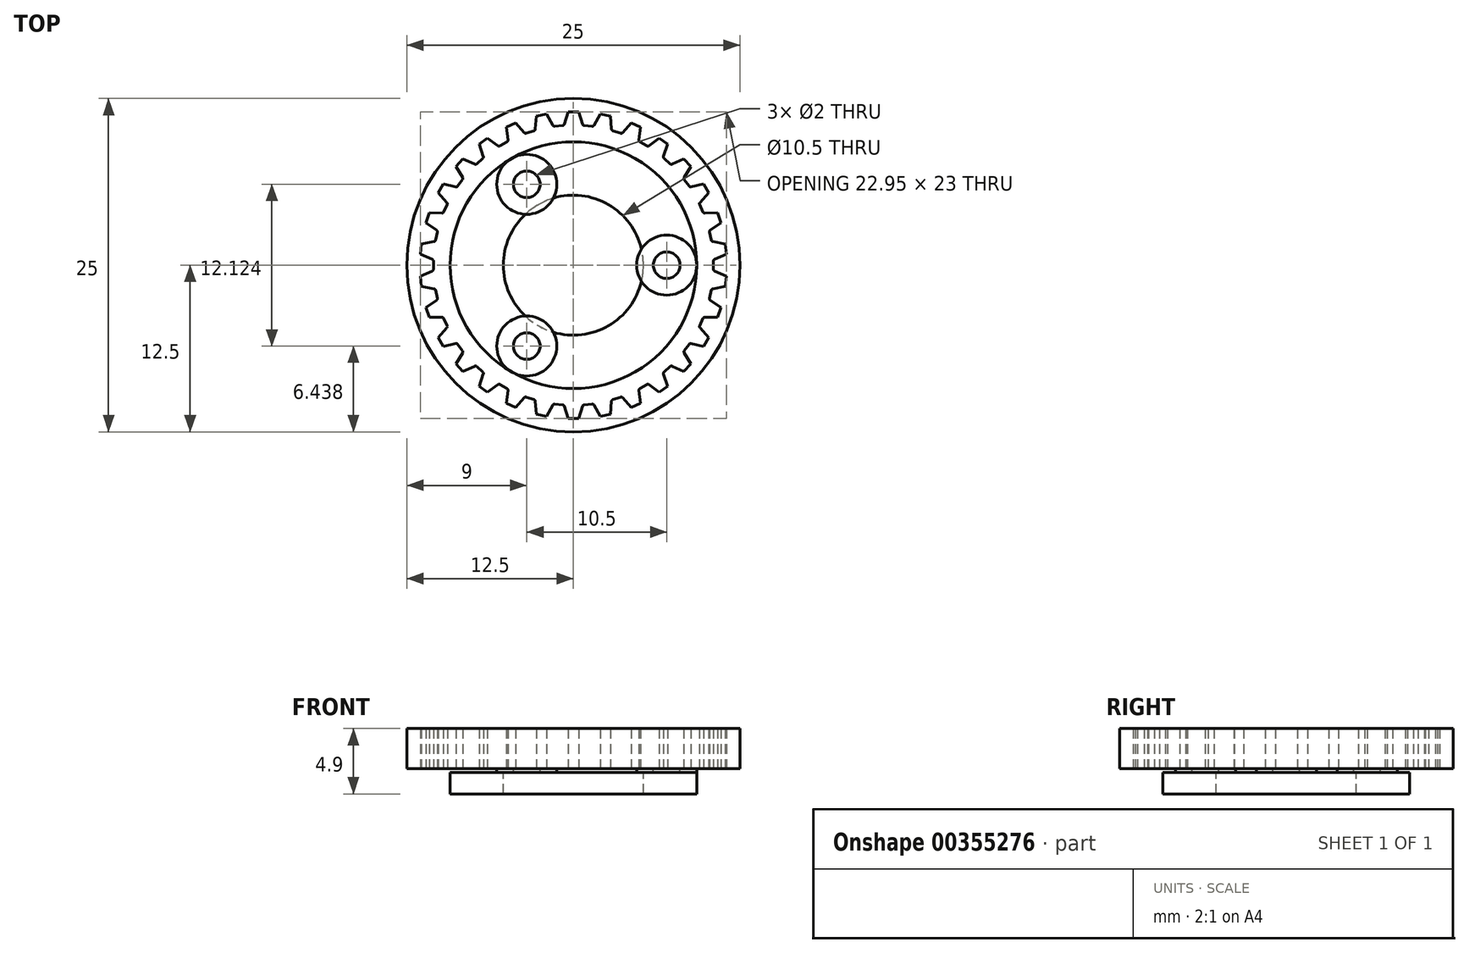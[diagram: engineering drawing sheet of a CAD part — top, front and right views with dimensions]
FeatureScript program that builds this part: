
annotation { "Feature Type Name" : "Feature", "Feature Type Description" : "" }
export const myFeature = defineFeature(function(context is Context, id is Id, definition is map)
    precondition{}
    {
        {
            assignVariable(context, id + "F0", {"name" : "THICK", "anyValue" : 3});
        }
        {
            var Q0;
            Q0=qCreatedBy(makeId("Top.planeOp"),FACE);
            var sketch = newSketch(context, id + "F1", { "sketchPlane" : qUnion([Q0])});
            skCircle(sketch, "E0", {"center": v(0, 0) * mm, "radius": 4 * mm});
            skCircle(sketch, "E1", {"center": v(0, 0) * mm, "radius": 3.5 * mm});
            skCircle(sketch, "E2", {"center": v(0, 0) * mm, "radius": 3 * mm});
            skSolve(sketch);
        }
        {
            var Q0;
            Q0=qCreatedBy(makeId("Top.planeOp"),FACE);
            var sketch = newSketch(context, id + "F2", { "sketchPlane" : qUnion([Q0])});
            skLineSegment(sketch, "E3", {"start": v(0, 0) * mm, "end": v(0, 4.84) * mm, "construction": true});
            skLineSegment(sketch, "E4", {"start": v(1.8, 5.57) * mm, "end": v(0, 0) * mm, "construction": true});
            skLineSegment(sketch, "E5", {"start": v(0.85, 5.38) * mm, "end": v(0, 0) * mm, "construction": true});
            skLineSegment(sketch, "E6", {"start": v(0, 4) * mm, "end": v(0.4, 4) * mm});
            skLineSegment(sketch, "E7", {"start": v(0.56, 3.86) * mm, "end": v(0.6, 2.96) * mm});
            skLineSegment(sketch, "E8", {"start": v(0.6, 2.96) * mm, "end": v(0.93, 2.85) * mm});
            skPoint(sketch, "E9.visualSharp", {"position": v(0.55, 4) * mm});
            skArc(sketch, "E9.filletArc", {"start": v(0.56, 3.86) * mm, "mid": v(0.51, 3.96) * mm, "end": v(0.4, 4) * mm});
            skLineSegment(sketch, "E10.MirrorCS", {"start": v(1.25, 2.75) * mm, "end": v(0.93, 2.85) * mm});
            skLineSegment(sketch, "E11.MirrorCS", {"start": v(2.35, 3.24) * mm, "end": v(2.02, 3.48) * mm});
            skLineSegment(sketch, "E12.MirrorCS", {"start": v(1.82, 3.45) * mm, "end": v(1.25, 2.75) * mm});
            skArc(sketch, "E13.MirrorCS", {"start": v(1.82, 3.45) * mm, "mid": v(1.91, 3.5) * mm, "end": v(2.02, 3.48) * mm});
            skLineSegment(sketch, "E14.1.0", {"start": v(-2.35, 3.24) * mm, "end": v(-2.02, 3.48) * mm});
            skArc(sketch, "E14.1.1", {"start": v(-1.82, 3.45) * mm, "mid": v(-1.91, 3.5) * mm, "end": v(-2.02, 3.48) * mm});
            skLineSegment(sketch, "E14.1.2", {"start": v(-1.82, 3.45) * mm, "end": v(-1.25, 2.75) * mm});
            skLineSegment(sketch, "E14.1.3", {"start": v(-1.25, 2.75) * mm, "end": v(-0.93, 2.85) * mm});
            skLineSegment(sketch, "E14.1.4", {"start": v(-0.6, 2.96) * mm, "end": v(-0.93, 2.85) * mm});
            skLineSegment(sketch, "E14.1.5", {"start": v(-0.56, 3.86) * mm, "end": v(-0.6, 2.96) * mm});
            skLineSegment(sketch, "E14.1.6", {"start": v(0, 4) * mm, "end": v(-0.4, 4) * mm});
            skArc(sketch, "E14.1.7", {"start": v(-0.56, 3.86) * mm, "mid": v(-0.51, 3.96) * mm, "end": v(-0.4, 4) * mm});
            skLineSegment(sketch, "E14.2.0", {"start": v(-3.8, 1.24) * mm, "end": v(-3.68, 1.62) * mm});
            skArc(sketch, "E14.2.1", {"start": v(-3.5, 1.72) * mm, "mid": v(-3.6, 1.7) * mm, "end": v(-3.68, 1.62) * mm});
            skLineSegment(sketch, "E14.2.2", {"start": v(-3.5, 1.72) * mm, "end": v(-2.63, 1.49) * mm});
            skLineSegment(sketch, "E14.2.3", {"start": v(-2.63, 1.49) * mm, "end": v(-2.43, 1.76) * mm});
            skLineSegment(sketch, "E14.2.4", {"start": v(-2.23, 2.04) * mm, "end": v(-2.43, 1.76) * mm});
            skLineSegment(sketch, "E14.2.5", {"start": v(-2.72, 2.8) * mm, "end": v(-2.23, 2.04) * mm});
            skLineSegment(sketch, "E14.2.6", {"start": v(-2.35, 3.24) * mm, "end": v(-2.68, 3) * mm});
            skArc(sketch, "E14.2.7", {"start": v(-2.72, 2.8) * mm, "mid": v(-2.74, 2.9) * mm, "end": v(-2.68, 3) * mm});
            skLineSegment(sketch, "E14.3.0", {"start": v(-3.8, -1.24) * mm, "end": v(-3.93, -0.85) * mm});
            skArc(sketch, "E14.3.1", {"start": v(-3.84, -0.66) * mm, "mid": v(-3.92, -0.74) * mm, "end": v(-3.93, -0.85) * mm});
            skLineSegment(sketch, "E14.3.2", {"start": v(-3.84, -0.66) * mm, "end": v(-3, -0.34) * mm});
            skLineSegment(sketch, "E14.3.3", {"start": v(-3, -0.34) * mm, "end": v(-3, 0) * mm});
            skLineSegment(sketch, "E14.3.4", {"start": v(-3, 0.34) * mm, "end": v(-3, 0) * mm});
            skLineSegment(sketch, "E14.3.5", {"start": v(-3.84, 0.66) * mm, "end": v(-3, 0.34) * mm});
            skLineSegment(sketch, "E14.3.6", {"start": v(-3.8, 1.24) * mm, "end": v(-3.93, 0.85) * mm});
            skArc(sketch, "E14.3.7", {"start": v(-3.84, 0.66) * mm, "mid": v(-3.92, 0.74) * mm, "end": v(-3.93, 0.85) * mm});
            skLineSegment(sketch, "E14.4.0", {"start": v(-2.35, -3.24) * mm, "end": v(-2.68, -3) * mm});
            skArc(sketch, "E14.4.1", {"start": v(-2.72, -2.8) * mm, "mid": v(-2.74, -2.9) * mm, "end": v(-2.68, -3) * mm});
            skLineSegment(sketch, "E14.4.2", {"start": v(-2.72, -2.8) * mm, "end": v(-2.23, -2.04) * mm});
            skLineSegment(sketch, "E14.4.3", {"start": v(-2.23, -2.04) * mm, "end": v(-2.43, -1.76) * mm});
            skLineSegment(sketch, "E14.4.4", {"start": v(-2.63, -1.49) * mm, "end": v(-2.43, -1.76) * mm});
            skLineSegment(sketch, "E14.4.5", {"start": v(-3.5, -1.72) * mm, "end": v(-2.63, -1.49) * mm});
            skLineSegment(sketch, "E14.4.6", {"start": v(-3.8, -1.24) * mm, "end": v(-3.68, -1.62) * mm});
            skArc(sketch, "E14.4.7", {"start": v(-3.5, -1.72) * mm, "mid": v(-3.6, -1.7) * mm, "end": v(-3.68, -1.62) * mm});
            skLineSegment(sketch, "E14.5.0", {"start": v(0, -4) * mm, "end": v(-0.4, -4) * mm});
            skArc(sketch, "E14.5.1", {"start": v(-0.56, -3.86) * mm, "mid": v(-0.51, -3.96) * mm, "end": v(-0.4, -4) * mm});
            skLineSegment(sketch, "E14.5.2", {"start": v(-0.56, -3.86) * mm, "end": v(-0.6, -2.96) * mm});
            skLineSegment(sketch, "E14.5.3", {"start": v(-0.6, -2.96) * mm, "end": v(-0.93, -2.85) * mm});
            skLineSegment(sketch, "E14.5.4", {"start": v(-1.25, -2.75) * mm, "end": v(-0.93, -2.85) * mm});
            skLineSegment(sketch, "E14.5.5", {"start": v(-1.82, -3.45) * mm, "end": v(-1.25, -2.75) * mm});
            skLineSegment(sketch, "E14.5.6", {"start": v(-2.35, -3.24) * mm, "end": v(-2.02, -3.48) * mm});
            skArc(sketch, "E14.5.7", {"start": v(-1.82, -3.45) * mm, "mid": v(-1.91, -3.5) * mm, "end": v(-2.02, -3.48) * mm});
            skLineSegment(sketch, "E14.6.0", {"start": v(2.35, -3.24) * mm, "end": v(2.02, -3.48) * mm});
            skArc(sketch, "E14.6.1", {"start": v(1.82, -3.45) * mm, "mid": v(1.91, -3.5) * mm, "end": v(2.02, -3.48) * mm});
            skLineSegment(sketch, "E14.6.2", {"start": v(1.82, -3.45) * mm, "end": v(1.25, -2.75) * mm});
            skLineSegment(sketch, "E14.6.3", {"start": v(1.25, -2.75) * mm, "end": v(0.93, -2.85) * mm});
            skLineSegment(sketch, "E14.6.4", {"start": v(0.6, -2.96) * mm, "end": v(0.93, -2.85) * mm});
            skLineSegment(sketch, "E14.6.5", {"start": v(0.56, -3.86) * mm, "end": v(0.6, -2.96) * mm});
            skLineSegment(sketch, "E14.6.6", {"start": v(0, -4) * mm, "end": v(0.4, -4) * mm});
            skArc(sketch, "E14.6.7", {"start": v(0.56, -3.86) * mm, "mid": v(0.51, -3.96) * mm, "end": v(0.4, -4) * mm});
            skLineSegment(sketch, "E14.7.0", {"start": v(3.8, -1.24) * mm, "end": v(3.68, -1.62) * mm});
            skArc(sketch, "E14.7.1", {"start": v(3.5, -1.72) * mm, "mid": v(3.6, -1.7) * mm, "end": v(3.68, -1.62) * mm});
            skLineSegment(sketch, "E14.7.2", {"start": v(3.5, -1.72) * mm, "end": v(2.63, -1.49) * mm});
            skLineSegment(sketch, "E14.7.3", {"start": v(2.63, -1.49) * mm, "end": v(2.43, -1.76) * mm});
            skLineSegment(sketch, "E14.7.4", {"start": v(2.23, -2.04) * mm, "end": v(2.43, -1.76) * mm});
            skLineSegment(sketch, "E14.7.5", {"start": v(2.72, -2.8) * mm, "end": v(2.23, -2.04) * mm});
            skLineSegment(sketch, "E14.7.6", {"start": v(2.35, -3.24) * mm, "end": v(2.68, -3) * mm});
            skArc(sketch, "E14.7.7", {"start": v(2.72, -2.8) * mm, "mid": v(2.74, -2.9) * mm, "end": v(2.68, -3) * mm});
            skLineSegment(sketch, "E14.8.0", {"start": v(3.8, 1.24) * mm, "end": v(3.93, 0.85) * mm});
            skArc(sketch, "E14.8.1", {"start": v(3.84, 0.66) * mm, "mid": v(3.92, 0.74) * mm, "end": v(3.93, 0.85) * mm});
            skLineSegment(sketch, "E14.8.2", {"start": v(3.84, 0.66) * mm, "end": v(3, 0.34) * mm});
            skLineSegment(sketch, "E14.8.3", {"start": v(3, 0.34) * mm, "end": v(3, 0) * mm});
            skLineSegment(sketch, "E14.8.4", {"start": v(3, -0.34) * mm, "end": v(3, 0) * mm});
            skLineSegment(sketch, "E14.8.5", {"start": v(3.84, -0.66) * mm, "end": v(3, -0.34) * mm});
            skLineSegment(sketch, "E14.8.6", {"start": v(3.8, -1.24) * mm, "end": v(3.93, -0.85) * mm});
            skArc(sketch, "E14.8.7", {"start": v(3.84, -0.66) * mm, "mid": v(3.92, -0.74) * mm, "end": v(3.93, -0.85) * mm});
            skLineSegment(sketch, "E14.9.0", {"start": v(2.35, 3.24) * mm, "end": v(2.68, 3) * mm});
            skArc(sketch, "E14.9.1", {"start": v(2.72, 2.8) * mm, "mid": v(2.74, 2.9) * mm, "end": v(2.68, 3) * mm});
            skLineSegment(sketch, "E14.9.2", {"start": v(2.72, 2.8) * mm, "end": v(2.23, 2.04) * mm});
            skLineSegment(sketch, "E14.9.3", {"start": v(2.23, 2.04) * mm, "end": v(2.43, 1.76) * mm});
            skLineSegment(sketch, "E14.9.4", {"start": v(2.63, 1.49) * mm, "end": v(2.43, 1.76) * mm});
            skLineSegment(sketch, "E14.9.5", {"start": v(3.5, 1.72) * mm, "end": v(2.63, 1.49) * mm});
            skLineSegment(sketch, "E14.9.6", {"start": v(3.8, 1.24) * mm, "end": v(3.68, 1.62) * mm});
            skArc(sketch, "E14.9.7", {"start": v(3.5, 1.72) * mm, "mid": v(3.6, 1.7) * mm, "end": v(3.68, 1.62) * mm});
            skPoint(sketch, "E14.center", {"position": v(0, 0) * mm});
            skSolve(sketch);
        }
        {
            var Q0;
            Q0=qSketchRegion(id+"F2",true);
            extrude(context, id + "F3", {"entities" : qUnion([Q0]), "depth" : (getVariable(context, 'THICK')) * mm});
        }
        {
            var Q0;
            Q0=makeQuery(id+"F3.opExtrude","CAP_FACE",FACE,{"disambiguationData":[OSD([sQuery(id+"F2.wireOp",EDGE,"E6"),sQuery(id+"F2.wireOp",EDGE,"E7"),sQuery(id+"F2.wireOp",EDGE,"E8"),sQuery(id+"F2.wireOp",EDGE,"E9.filletArc"),sQuery(id+"F2.wireOp",EDGE,"E10.MirrorCS"),sQuery(id+"F2.wireOp",EDGE,"E11.MirrorCS"),sQuery(id+"F2.wireOp",EDGE,"E12.MirrorCS"),sQuery(id+"F2.wireOp",EDGE,"E13.MirrorCS"),sQuery(id+"F2.wireOp",EDGE,"E14.1.0"),sQuery(id+"F2.wireOp",EDGE,"E14.1.1"),sQuery(id+"F2.wireOp",EDGE,"E14.1.2"),sQuery(id+"F2.wireOp",EDGE,"E14.1.3"),sQuery(id+"F2.wireOp",EDGE,"E14.1.4"),sQuery(id+"F2.wireOp",EDGE,"E14.1.5"),sQuery(id+"F2.wireOp",EDGE,"E14.1.6"),sQuery(id+"F2.wireOp",EDGE,"E14.1.7"),sQuery(id+"F2.wireOp",EDGE,"E14.2.0"),sQuery(id+"F2.wireOp",EDGE,"E14.2.1"),sQuery(id+"F2.wireOp",EDGE,"E14.2.2"),sQuery(id+"F2.wireOp",EDGE,"E14.2.3"),sQuery(id+"F2.wireOp",EDGE,"E14.2.4"),sQuery(id+"F2.wireOp",EDGE,"E14.2.5"),sQuery(id+"F2.wireOp",EDGE,"E14.2.6"),sQuery(id+"F2.wireOp",EDGE,"E14.2.7"),sQuery(id+"F2.wireOp",EDGE,"E14.3.0"),sQuery(id+"F2.wireOp",EDGE,"E14.3.1"),sQuery(id+"F2.wireOp",EDGE,"E14.3.2"),sQuery(id+"F2.wireOp",EDGE,"E14.3.3"),sQuery(id+"F2.wireOp",EDGE,"E14.3.4"),sQuery(id+"F2.wireOp",EDGE,"E14.3.5"),sQuery(id+"F2.wireOp",EDGE,"E14.3.6"),sQuery(id+"F2.wireOp",EDGE,"E14.3.7"),sQuery(id+"F2.wireOp",EDGE,"E14.4.0"),sQuery(id+"F2.wireOp",EDGE,"E14.4.1"),sQuery(id+"F2.wireOp",EDGE,"E14.4.2"),sQuery(id+"F2.wireOp",EDGE,"E14.4.3"),sQuery(id+"F2.wireOp",EDGE,"E14.4.4"),sQuery(id+"F2.wireOp",EDGE,"E14.4.5"),sQuery(id+"F2.wireOp",EDGE,"E14.4.6"),sQuery(id+"F2.wireOp",EDGE,"E14.4.7"),sQuery(id+"F2.wireOp",EDGE,"E14.5.0"),sQuery(id+"F2.wireOp",EDGE,"E14.5.1"),sQuery(id+"F2.wireOp",EDGE,"E14.5.2"),sQuery(id+"F2.wireOp",EDGE,"E14.5.3"),sQuery(id+"F2.wireOp",EDGE,"E14.5.4"),sQuery(id+"F2.wireOp",EDGE,"E14.5.5"),sQuery(id+"F2.wireOp",EDGE,"E14.5.6"),sQuery(id+"F2.wireOp",EDGE,"E14.5.7"),sQuery(id+"F2.wireOp",EDGE,"E14.6.0"),sQuery(id+"F2.wireOp",EDGE,"E14.6.1"),sQuery(id+"F2.wireOp",EDGE,"E14.6.2"),sQuery(id+"F2.wireOp",EDGE,"E14.6.3"),sQuery(id+"F2.wireOp",EDGE,"E14.6.4"),sQuery(id+"F2.wireOp",EDGE,"E14.6.5"),sQuery(id+"F2.wireOp",EDGE,"E14.6.6"),sQuery(id+"F2.wireOp",EDGE,"E14.6.7"),sQuery(id+"F2.wireOp",EDGE,"E14.7.0"),sQuery(id+"F2.wireOp",EDGE,"E14.7.1"),sQuery(id+"F2.wireOp",EDGE,"E14.7.2"),sQuery(id+"F2.wireOp",EDGE,"E14.7.3"),sQuery(id+"F2.wireOp",EDGE,"E14.7.4"),sQuery(id+"F2.wireOp",EDGE,"E14.7.5"),sQuery(id+"F2.wireOp",EDGE,"E14.7.6"),sQuery(id+"F2.wireOp",EDGE,"E14.7.7"),sQuery(id+"F2.wireOp",EDGE,"E14.8.0"),sQuery(id+"F2.wireOp",EDGE,"E14.8.1"),sQuery(id+"F2.wireOp",EDGE,"E14.8.2"),sQuery(id+"F2.wireOp",EDGE,"E14.8.3"),sQuery(id+"F2.wireOp",EDGE,"E14.8.4"),sQuery(id+"F2.wireOp",EDGE,"E14.8.5"),sQuery(id+"F2.wireOp",EDGE,"E14.8.6"),sQuery(id+"F2.wireOp",EDGE,"E14.8.7"),sQuery(id+"F2.wireOp",EDGE,"E14.9.0"),sQuery(id+"F2.wireOp",EDGE,"E14.9.1"),sQuery(id+"F2.wireOp",EDGE,"E14.9.2"),sQuery(id+"F2.wireOp",EDGE,"E14.9.3"),sQuery(id+"F2.wireOp",EDGE,"E14.9.4"),sQuery(id+"F2.wireOp",EDGE,"E14.9.5"),sQuery(id+"F2.wireOp",EDGE,"E14.9.6"),sQuery(id+"F2.wireOp",EDGE,"E14.9.7")])],"isStart":true});
            var sketch = newSketch(context, id + "F4", { "sketchPlane" : qUnion([Q0])});
            skCircle(sketch, "E15", {"center": v(0, 0) * mm, "radius": 2.25 * mm});
            skSolve(sketch);
        }
        {
            var Q0;
            Q0=qSketchRegion(id+"F4",true);
            extrude(context, id + "F5", {"entities" : qUnion([Q0]), "operationType" : NewBodyOperationType.ADD, "depth" : 0.3 * mm});
        }
        {
            var Q0;
            Q0=makeQuery(id+"F3.opExtrude","SWEPT_BODY",BODY,{"disambiguationData":[OSD([sQuery(id+"F2.wireOp",EDGE,"E6"),sQuery(id+"F2.wireOp",EDGE,"E7"),sQuery(id+"F2.wireOp",EDGE,"E8"),sQuery(id+"F2.wireOp",EDGE,"E9.filletArc"),sQuery(id+"F2.wireOp",EDGE,"E10.MirrorCS"),sQuery(id+"F2.wireOp",EDGE,"E11.MirrorCS"),sQuery(id+"F2.wireOp",EDGE,"E12.MirrorCS"),sQuery(id+"F2.wireOp",EDGE,"E13.MirrorCS"),sQuery(id+"F2.wireOp",EDGE,"E14.1.0"),sQuery(id+"F2.wireOp",EDGE,"E14.1.1"),sQuery(id+"F2.wireOp",EDGE,"E14.1.2"),sQuery(id+"F2.wireOp",EDGE,"E14.1.3"),sQuery(id+"F2.wireOp",EDGE,"E14.1.4"),sQuery(id+"F2.wireOp",EDGE,"E14.1.5"),sQuery(id+"F2.wireOp",EDGE,"E14.1.6"),sQuery(id+"F2.wireOp",EDGE,"E14.1.7"),sQuery(id+"F2.wireOp",EDGE,"E14.2.0"),sQuery(id+"F2.wireOp",EDGE,"E14.2.1"),sQuery(id+"F2.wireOp",EDGE,"E14.2.2"),sQuery(id+"F2.wireOp",EDGE,"E14.2.3"),sQuery(id+"F2.wireOp",EDGE,"E14.2.4"),sQuery(id+"F2.wireOp",EDGE,"E14.2.5"),sQuery(id+"F2.wireOp",EDGE,"E14.2.6"),sQuery(id+"F2.wireOp",EDGE,"E14.2.7"),sQuery(id+"F2.wireOp",EDGE,"E14.3.0"),sQuery(id+"F2.wireOp",EDGE,"E14.3.1"),sQuery(id+"F2.wireOp",EDGE,"E14.3.2"),sQuery(id+"F2.wireOp",EDGE,"E14.3.3"),sQuery(id+"F2.wireOp",EDGE,"E14.3.4"),sQuery(id+"F2.wireOp",EDGE,"E14.3.5"),sQuery(id+"F2.wireOp",EDGE,"E14.3.6"),sQuery(id+"F2.wireOp",EDGE,"E14.3.7"),sQuery(id+"F2.wireOp",EDGE,"E14.4.0"),sQuery(id+"F2.wireOp",EDGE,"E14.4.1"),sQuery(id+"F2.wireOp",EDGE,"E14.4.2"),sQuery(id+"F2.wireOp",EDGE,"E14.4.3"),sQuery(id+"F2.wireOp",EDGE,"E14.4.4"),sQuery(id+"F2.wireOp",EDGE,"E14.4.5"),sQuery(id+"F2.wireOp",EDGE,"E14.4.6"),sQuery(id+"F2.wireOp",EDGE,"E14.4.7"),sQuery(id+"F2.wireOp",EDGE,"E14.5.0"),sQuery(id+"F2.wireOp",EDGE,"E14.5.1"),sQuery(id+"F2.wireOp",EDGE,"E14.5.2"),sQuery(id+"F2.wireOp",EDGE,"E14.5.3"),sQuery(id+"F2.wireOp",EDGE,"E14.5.4"),sQuery(id+"F2.wireOp",EDGE,"E14.5.5"),sQuery(id+"F2.wireOp",EDGE,"E14.5.6"),sQuery(id+"F2.wireOp",EDGE,"E14.5.7"),sQuery(id+"F2.wireOp",EDGE,"E14.6.0"),sQuery(id+"F2.wireOp",EDGE,"E14.6.1"),sQuery(id+"F2.wireOp",EDGE,"E14.6.2"),sQuery(id+"F2.wireOp",EDGE,"E14.6.3"),sQuery(id+"F2.wireOp",EDGE,"E14.6.4"),sQuery(id+"F2.wireOp",EDGE,"E14.6.5"),sQuery(id+"F2.wireOp",EDGE,"E14.6.6"),sQuery(id+"F2.wireOp",EDGE,"E14.6.7"),sQuery(id+"F2.wireOp",EDGE,"E14.7.0"),sQuery(id+"F2.wireOp",EDGE,"E14.7.1"),sQuery(id+"F2.wireOp",EDGE,"E14.7.2"),sQuery(id+"F2.wireOp",EDGE,"E14.7.3"),sQuery(id+"F2.wireOp",EDGE,"E14.7.4"),sQuery(id+"F2.wireOp",EDGE,"E14.7.5"),sQuery(id+"F2.wireOp",EDGE,"E14.7.6"),sQuery(id+"F2.wireOp",EDGE,"E14.7.7"),sQuery(id+"F2.wireOp",EDGE,"E14.8.0"),sQuery(id+"F2.wireOp",EDGE,"E14.8.1"),sQuery(id+"F2.wireOp",EDGE,"E14.8.2"),sQuery(id+"F2.wireOp",EDGE,"E14.8.3"),sQuery(id+"F2.wireOp",EDGE,"E14.8.4"),sQuery(id+"F2.wireOp",EDGE,"E14.8.5"),sQuery(id+"F2.wireOp",EDGE,"E14.8.6"),sQuery(id+"F2.wireOp",EDGE,"E14.8.7"),sQuery(id+"F2.wireOp",EDGE,"E14.9.0"),sQuery(id+"F2.wireOp",EDGE,"E14.9.1"),sQuery(id+"F2.wireOp",EDGE,"E14.9.2"),sQuery(id+"F2.wireOp",EDGE,"E14.9.3"),sQuery(id+"F2.wireOp",EDGE,"E14.9.4"),sQuery(id+"F2.wireOp",EDGE,"E14.9.5"),sQuery(id+"F2.wireOp",EDGE,"E14.9.6"),sQuery(id+"F2.wireOp",EDGE,"E14.9.7")])]});
            transform(context, id + "F6", {"entities" : qUnion([Q0]), "transformType" : TransformType.COPY});
        }
        {
            var Q0;
            Q0=makeQuery(id+"F3.opExtrude","CAP_FACE",FACE,{"disambiguationData":[OSD([sQuery(id+"F2.wireOp",EDGE,"E6"),sQuery(id+"F2.wireOp",EDGE,"E7"),sQuery(id+"F2.wireOp",EDGE,"E8"),sQuery(id+"F2.wireOp",EDGE,"E9.filletArc"),sQuery(id+"F2.wireOp",EDGE,"E10.MirrorCS"),sQuery(id+"F2.wireOp",EDGE,"E11.MirrorCS"),sQuery(id+"F2.wireOp",EDGE,"E12.MirrorCS"),sQuery(id+"F2.wireOp",EDGE,"E13.MirrorCS"),sQuery(id+"F2.wireOp",EDGE,"E14.1.0"),sQuery(id+"F2.wireOp",EDGE,"E14.1.1"),sQuery(id+"F2.wireOp",EDGE,"E14.1.2"),sQuery(id+"F2.wireOp",EDGE,"E14.1.3"),sQuery(id+"F2.wireOp",EDGE,"E14.1.4"),sQuery(id+"F2.wireOp",EDGE,"E14.1.5"),sQuery(id+"F2.wireOp",EDGE,"E14.1.6"),sQuery(id+"F2.wireOp",EDGE,"E14.1.7"),sQuery(id+"F2.wireOp",EDGE,"E14.2.0"),sQuery(id+"F2.wireOp",EDGE,"E14.2.1"),sQuery(id+"F2.wireOp",EDGE,"E14.2.2"),sQuery(id+"F2.wireOp",EDGE,"E14.2.3"),sQuery(id+"F2.wireOp",EDGE,"E14.2.4"),sQuery(id+"F2.wireOp",EDGE,"E14.2.5"),sQuery(id+"F2.wireOp",EDGE,"E14.2.6"),sQuery(id+"F2.wireOp",EDGE,"E14.2.7"),sQuery(id+"F2.wireOp",EDGE,"E14.3.0"),sQuery(id+"F2.wireOp",EDGE,"E14.3.1"),sQuery(id+"F2.wireOp",EDGE,"E14.3.2"),sQuery(id+"F2.wireOp",EDGE,"E14.3.3"),sQuery(id+"F2.wireOp",EDGE,"E14.3.4"),sQuery(id+"F2.wireOp",EDGE,"E14.3.5"),sQuery(id+"F2.wireOp",EDGE,"E14.3.6"),sQuery(id+"F2.wireOp",EDGE,"E14.3.7"),sQuery(id+"F2.wireOp",EDGE,"E14.4.0"),sQuery(id+"F2.wireOp",EDGE,"E14.4.1"),sQuery(id+"F2.wireOp",EDGE,"E14.4.2"),sQuery(id+"F2.wireOp",EDGE,"E14.4.3"),sQuery(id+"F2.wireOp",EDGE,"E14.4.4"),sQuery(id+"F2.wireOp",EDGE,"E14.4.5"),sQuery(id+"F2.wireOp",EDGE,"E14.4.6"),sQuery(id+"F2.wireOp",EDGE,"E14.4.7"),sQuery(id+"F2.wireOp",EDGE,"E14.5.0"),sQuery(id+"F2.wireOp",EDGE,"E14.5.1"),sQuery(id+"F2.wireOp",EDGE,"E14.5.2"),sQuery(id+"F2.wireOp",EDGE,"E14.5.3"),sQuery(id+"F2.wireOp",EDGE,"E14.5.4"),sQuery(id+"F2.wireOp",EDGE,"E14.5.5"),sQuery(id+"F2.wireOp",EDGE,"E14.5.6"),sQuery(id+"F2.wireOp",EDGE,"E14.5.7"),sQuery(id+"F2.wireOp",EDGE,"E14.6.0"),sQuery(id+"F2.wireOp",EDGE,"E14.6.1"),sQuery(id+"F2.wireOp",EDGE,"E14.6.2"),sQuery(id+"F2.wireOp",EDGE,"E14.6.3"),sQuery(id+"F2.wireOp",EDGE,"E14.6.4"),sQuery(id+"F2.wireOp",EDGE,"E14.6.5"),sQuery(id+"F2.wireOp",EDGE,"E14.6.6"),sQuery(id+"F2.wireOp",EDGE,"E14.6.7"),sQuery(id+"F2.wireOp",EDGE,"E14.7.0"),sQuery(id+"F2.wireOp",EDGE,"E14.7.1"),sQuery(id+"F2.wireOp",EDGE,"E14.7.2"),sQuery(id+"F2.wireOp",EDGE,"E14.7.3"),sQuery(id+"F2.wireOp",EDGE,"E14.7.4"),sQuery(id+"F2.wireOp",EDGE,"E14.7.5"),sQuery(id+"F2.wireOp",EDGE,"E14.7.6"),sQuery(id+"F2.wireOp",EDGE,"E14.7.7"),sQuery(id+"F2.wireOp",EDGE,"E14.8.0"),sQuery(id+"F2.wireOp",EDGE,"E14.8.1"),sQuery(id+"F2.wireOp",EDGE,"E14.8.2"),sQuery(id+"F2.wireOp",EDGE,"E14.8.3"),sQuery(id+"F2.wireOp",EDGE,"E14.8.4"),sQuery(id+"F2.wireOp",EDGE,"E14.8.5"),sQuery(id+"F2.wireOp",EDGE,"E14.8.6"),sQuery(id+"F2.wireOp",EDGE,"E14.8.7"),sQuery(id+"F2.wireOp",EDGE,"E14.9.0"),sQuery(id+"F2.wireOp",EDGE,"E14.9.1"),sQuery(id+"F2.wireOp",EDGE,"E14.9.2"),sQuery(id+"F2.wireOp",EDGE,"E14.9.3"),sQuery(id+"F2.wireOp",EDGE,"E14.9.4"),sQuery(id+"F2.wireOp",EDGE,"E14.9.5"),sQuery(id+"F2.wireOp",EDGE,"E14.9.6"),sQuery(id+"F2.wireOp",EDGE,"E14.9.7")])],"isStart":false});
            var sketch = newSketch(context, id + "F7", { "sketchPlane" : qUnion([Q0])});
            skCircle(sketch, "E16.cCircle", {"center": v(0, 0) * mm, "radius": 0.86 * mm, "construction": true});
            skLineSegment(sketch, "E16.0", {"start": v(0.86, 0.5) * mm, "end": v(0.86, -0.5) * mm});
            skLineSegment(sketch, "E16.1", {"start": v(0.86, -0.5) * mm, "end": v(0, -1) * mm});
            skLineSegment(sketch, "E16.2", {"start": v(0, -1) * mm, "end": v(-0.86, -0.5) * mm});
            skLineSegment(sketch, "E16.3", {"start": v(-0.86, -0.5) * mm, "end": v(-0.86, 0.5) * mm});
            skLineSegment(sketch, "E16.4", {"start": v(-0.86, 0.5) * mm, "end": v(0, 1) * mm});
            skLineSegment(sketch, "E16.5", {"start": v(0, 1) * mm, "end": v(0.86, 0.5) * mm});
            skPoint(sketch, "E16.0.midPoint", {"position": v(0.86, 0) * mm});
            skSolve(sketch);
        }
        {
            var Q0;
            Q0=qSketchRegion(id+"F7",true);
            extrude(context, id + "F8", {"entities" : qUnion([Q0]), "operationType" : NewBodyOperationType.REMOVE, "oppositeDirection" : true, "depth" : 25 * mm});
        }
        {
            var Q0;
            Q0=makeQuery(id+"F3.opExtrude","CAP_FACE",FACE,{"disambiguationData":[OSD([sQuery(id+"F2.wireOp",EDGE,"E6"),sQuery(id+"F2.wireOp",EDGE,"E7"),sQuery(id+"F2.wireOp",EDGE,"E8"),sQuery(id+"F2.wireOp",EDGE,"E9.filletArc"),sQuery(id+"F2.wireOp",EDGE,"E10.MirrorCS"),sQuery(id+"F2.wireOp",EDGE,"E11.MirrorCS"),sQuery(id+"F2.wireOp",EDGE,"E12.MirrorCS"),sQuery(id+"F2.wireOp",EDGE,"E13.MirrorCS"),sQuery(id+"F2.wireOp",EDGE,"E14.1.0"),sQuery(id+"F2.wireOp",EDGE,"E14.1.1"),sQuery(id+"F2.wireOp",EDGE,"E14.1.2"),sQuery(id+"F2.wireOp",EDGE,"E14.1.3"),sQuery(id+"F2.wireOp",EDGE,"E14.1.4"),sQuery(id+"F2.wireOp",EDGE,"E14.1.5"),sQuery(id+"F2.wireOp",EDGE,"E14.1.6"),sQuery(id+"F2.wireOp",EDGE,"E14.1.7"),sQuery(id+"F2.wireOp",EDGE,"E14.2.0"),sQuery(id+"F2.wireOp",EDGE,"E14.2.1"),sQuery(id+"F2.wireOp",EDGE,"E14.2.2"),sQuery(id+"F2.wireOp",EDGE,"E14.2.3"),sQuery(id+"F2.wireOp",EDGE,"E14.2.4"),sQuery(id+"F2.wireOp",EDGE,"E14.2.5"),sQuery(id+"F2.wireOp",EDGE,"E14.2.6"),sQuery(id+"F2.wireOp",EDGE,"E14.2.7"),sQuery(id+"F2.wireOp",EDGE,"E14.3.0"),sQuery(id+"F2.wireOp",EDGE,"E14.3.1"),sQuery(id+"F2.wireOp",EDGE,"E14.3.2"),sQuery(id+"F2.wireOp",EDGE,"E14.3.3"),sQuery(id+"F2.wireOp",EDGE,"E14.3.4"),sQuery(id+"F2.wireOp",EDGE,"E14.3.5"),sQuery(id+"F2.wireOp",EDGE,"E14.3.6"),sQuery(id+"F2.wireOp",EDGE,"E14.3.7"),sQuery(id+"F2.wireOp",EDGE,"E14.4.0"),sQuery(id+"F2.wireOp",EDGE,"E14.4.1"),sQuery(id+"F2.wireOp",EDGE,"E14.4.2"),sQuery(id+"F2.wireOp",EDGE,"E14.4.3"),sQuery(id+"F2.wireOp",EDGE,"E14.4.4"),sQuery(id+"F2.wireOp",EDGE,"E14.4.5"),sQuery(id+"F2.wireOp",EDGE,"E14.4.6"),sQuery(id+"F2.wireOp",EDGE,"E14.4.7"),sQuery(id+"F2.wireOp",EDGE,"E14.5.0"),sQuery(id+"F2.wireOp",EDGE,"E14.5.1"),sQuery(id+"F2.wireOp",EDGE,"E14.5.2"),sQuery(id+"F2.wireOp",EDGE,"E14.5.3"),sQuery(id+"F2.wireOp",EDGE,"E14.5.4"),sQuery(id+"F2.wireOp",EDGE,"E14.5.5"),sQuery(id+"F2.wireOp",EDGE,"E14.5.6"),sQuery(id+"F2.wireOp",EDGE,"E14.5.7"),sQuery(id+"F2.wireOp",EDGE,"E14.6.0"),sQuery(id+"F2.wireOp",EDGE,"E14.6.1"),sQuery(id+"F2.wireOp",EDGE,"E14.6.2"),sQuery(id+"F2.wireOp",EDGE,"E14.6.3"),sQuery(id+"F2.wireOp",EDGE,"E14.6.4"),sQuery(id+"F2.wireOp",EDGE,"E14.6.5"),sQuery(id+"F2.wireOp",EDGE,"E14.6.6"),sQuery(id+"F2.wireOp",EDGE,"E14.6.7"),sQuery(id+"F2.wireOp",EDGE,"E14.7.0"),sQuery(id+"F2.wireOp",EDGE,"E14.7.1"),sQuery(id+"F2.wireOp",EDGE,"E14.7.2"),sQuery(id+"F2.wireOp",EDGE,"E14.7.3"),sQuery(id+"F2.wireOp",EDGE,"E14.7.4"),sQuery(id+"F2.wireOp",EDGE,"E14.7.5"),sQuery(id+"F2.wireOp",EDGE,"E14.7.6"),sQuery(id+"F2.wireOp",EDGE,"E14.7.7"),sQuery(id+"F2.wireOp",EDGE,"E14.8.0"),sQuery(id+"F2.wireOp",EDGE,"E14.8.1"),sQuery(id+"F2.wireOp",EDGE,"E14.8.2"),sQuery(id+"F2.wireOp",EDGE,"E14.8.3"),sQuery(id+"F2.wireOp",EDGE,"E14.8.4"),sQuery(id+"F2.wireOp",EDGE,"E14.8.5"),sQuery(id+"F2.wireOp",EDGE,"E14.8.6"),sQuery(id+"F2.wireOp",EDGE,"E14.8.7"),sQuery(id+"F2.wireOp",EDGE,"E14.9.0"),sQuery(id+"F2.wireOp",EDGE,"E14.9.1"),sQuery(id+"F2.wireOp",EDGE,"E14.9.2"),sQuery(id+"F2.wireOp",EDGE,"E14.9.3"),sQuery(id+"F2.wireOp",EDGE,"E14.9.4"),sQuery(id+"F2.wireOp",EDGE,"E14.9.5"),sQuery(id+"F2.wireOp",EDGE,"E14.9.6"),sQuery(id+"F2.wireOp",EDGE,"E14.9.7")])],"isStart":false});
            var sketch = newSketch(context, id + "F9", { "sketchPlane" : qUnion([Q0])});
            skCircle(sketch, "E17", {"center": v(0, 0) * mm, "radius": 1 * mm});
            skSolve(sketch);
        }
        {
            var Q0;
            Q0=qSketchRegion(id+"F9",true);
            extrude(context, id + "F10", {"entities" : qUnion([Q0]), "operationType" : NewBodyOperationType.REMOVE, "oppositeDirection" : true, "depth" : 25 * mm});
        }
        {
            var Q0;
            Q0=makeQuery(id+"F6.opPattern","COPY",BODY,{"derivedFrom":makeQuery(id+"F3.opExtrude","SWEPT_BODY",BODY,{"disambiguationData":[OSD([sQuery(id+"F2.wireOp",EDGE,"E6"),sQuery(id+"F2.wireOp",EDGE,"E7"),sQuery(id+"F2.wireOp",EDGE,"E8"),sQuery(id+"F2.wireOp",EDGE,"E9.filletArc"),sQuery(id+"F2.wireOp",EDGE,"E10.MirrorCS"),sQuery(id+"F2.wireOp",EDGE,"E11.MirrorCS"),sQuery(id+"F2.wireOp",EDGE,"E12.MirrorCS"),sQuery(id+"F2.wireOp",EDGE,"E13.MirrorCS"),sQuery(id+"F2.wireOp",EDGE,"E14.1.0"),sQuery(id+"F2.wireOp",EDGE,"E14.1.1"),sQuery(id+"F2.wireOp",EDGE,"E14.1.2"),sQuery(id+"F2.wireOp",EDGE,"E14.1.3"),sQuery(id+"F2.wireOp",EDGE,"E14.1.4"),sQuery(id+"F2.wireOp",EDGE,"E14.1.5"),sQuery(id+"F2.wireOp",EDGE,"E14.1.6"),sQuery(id+"F2.wireOp",EDGE,"E14.1.7"),sQuery(id+"F2.wireOp",EDGE,"E14.2.0"),sQuery(id+"F2.wireOp",EDGE,"E14.2.1"),sQuery(id+"F2.wireOp",EDGE,"E14.2.2"),sQuery(id+"F2.wireOp",EDGE,"E14.2.3"),sQuery(id+"F2.wireOp",EDGE,"E14.2.4"),sQuery(id+"F2.wireOp",EDGE,"E14.2.5"),sQuery(id+"F2.wireOp",EDGE,"E14.2.6"),sQuery(id+"F2.wireOp",EDGE,"E14.2.7"),sQuery(id+"F2.wireOp",EDGE,"E14.3.0"),sQuery(id+"F2.wireOp",EDGE,"E14.3.1"),sQuery(id+"F2.wireOp",EDGE,"E14.3.2"),sQuery(id+"F2.wireOp",EDGE,"E14.3.3"),sQuery(id+"F2.wireOp",EDGE,"E14.3.4"),sQuery(id+"F2.wireOp",EDGE,"E14.3.5"),sQuery(id+"F2.wireOp",EDGE,"E14.3.6"),sQuery(id+"F2.wireOp",EDGE,"E14.3.7"),sQuery(id+"F2.wireOp",EDGE,"E14.4.0"),sQuery(id+"F2.wireOp",EDGE,"E14.4.1"),sQuery(id+"F2.wireOp",EDGE,"E14.4.2"),sQuery(id+"F2.wireOp",EDGE,"E14.4.3"),sQuery(id+"F2.wireOp",EDGE,"E14.4.4"),sQuery(id+"F2.wireOp",EDGE,"E14.4.5"),sQuery(id+"F2.wireOp",EDGE,"E14.4.6"),sQuery(id+"F2.wireOp",EDGE,"E14.4.7"),sQuery(id+"F2.wireOp",EDGE,"E14.5.0"),sQuery(id+"F2.wireOp",EDGE,"E14.5.1"),sQuery(id+"F2.wireOp",EDGE,"E14.5.2"),sQuery(id+"F2.wireOp",EDGE,"E14.5.3"),sQuery(id+"F2.wireOp",EDGE,"E14.5.4"),sQuery(id+"F2.wireOp",EDGE,"E14.5.5"),sQuery(id+"F2.wireOp",EDGE,"E14.5.6"),sQuery(id+"F2.wireOp",EDGE,"E14.5.7"),sQuery(id+"F2.wireOp",EDGE,"E14.6.0"),sQuery(id+"F2.wireOp",EDGE,"E14.6.1"),sQuery(id+"F2.wireOp",EDGE,"E14.6.2"),sQuery(id+"F2.wireOp",EDGE,"E14.6.3"),sQuery(id+"F2.wireOp",EDGE,"E14.6.4"),sQuery(id+"F2.wireOp",EDGE,"E14.6.5"),sQuery(id+"F2.wireOp",EDGE,"E14.6.6"),sQuery(id+"F2.wireOp",EDGE,"E14.6.7"),sQuery(id+"F2.wireOp",EDGE,"E14.7.0"),sQuery(id+"F2.wireOp",EDGE,"E14.7.1"),sQuery(id+"F2.wireOp",EDGE,"E14.7.2"),sQuery(id+"F2.wireOp",EDGE,"E14.7.3"),sQuery(id+"F2.wireOp",EDGE,"E14.7.4"),sQuery(id+"F2.wireOp",EDGE,"E14.7.5"),sQuery(id+"F2.wireOp",EDGE,"E14.7.6"),sQuery(id+"F2.wireOp",EDGE,"E14.7.7"),sQuery(id+"F2.wireOp",EDGE,"E14.8.0"),sQuery(id+"F2.wireOp",EDGE,"E14.8.1"),sQuery(id+"F2.wireOp",EDGE,"E14.8.2"),sQuery(id+"F2.wireOp",EDGE,"E14.8.3"),sQuery(id+"F2.wireOp",EDGE,"E14.8.4"),sQuery(id+"F2.wireOp",EDGE,"E14.8.5"),sQuery(id+"F2.wireOp",EDGE,"E14.8.6"),sQuery(id+"F2.wireOp",EDGE,"E14.8.7"),sQuery(id+"F2.wireOp",EDGE,"E14.9.0"),sQuery(id+"F2.wireOp",EDGE,"E14.9.1"),sQuery(id+"F2.wireOp",EDGE,"E14.9.2"),sQuery(id+"F2.wireOp",EDGE,"E14.9.3"),sQuery(id+"F2.wireOp",EDGE,"E14.9.4"),sQuery(id+"F2.wireOp",EDGE,"E14.9.5"),sQuery(id+"F2.wireOp",EDGE,"E14.9.6"),sQuery(id+"F2.wireOp",EDGE,"E14.9.7")])]}),"instanceName":"1"});
            transform(context, id + "F11", {"entities" : qUnion([Q0]), "transformType" : TransformType.COPY});
        }
        {
            var Q0;
            Q0=qCreatedBy(makeId("Top.planeOp"),FACE);
            var sketch = newSketch(context, id + "F12", { "sketchPlane" : qUnion([Q0])});
            skCircle(sketch, "E18", {"center": v(0, 0) * mm, "radius": 10.5 * mm});
            skCircle(sketch, "E19", {"center": v(0, 0) * mm, "radius": 11 * mm});
            skCircle(sketch, "E20.0", {"center": v(0, 0) * mm, "radius": 11.5 * mm});
            skSolve(sketch);
        }
        {
            var Q0;
            Q0=qCreatedBy(makeId("Top.planeOp"),FACE);
            var sketch = newSketch(context, id + "F13", { "sketchPlane" : qUnion([Q0])});
            skLineSegment(sketch, "E21", {"start": v(0, 0) * mm, "end": v(0, 15.18) * mm, "construction": true});
            skLineSegment(sketch, "E22", {"start": v(1.56, 14.86) * mm, "end": v(0, 0) * mm, "construction": true});
            skLineSegment(sketch, "E23", {"start": v(0, 0) * mm, "end": v(0.84, 15.95) * mm, "construction": true});
            skLineSegment(sketch, "E24", {"start": v(0, 11.5) * mm, "end": v(0.39, 11.5) * mm});
            skLineSegment(sketch, "E25", {"start": v(0.39, 11.5) * mm, "end": v(0.67, 10.58) * mm});
            skLineSegment(sketch, "E26", {"start": v(0.8, 10.47) * mm, "end": v(1.1, 10.44) * mm});
            skPoint(sketch, "E27.visualSharp", {"position": v(0.7, 10.48) * mm});
            skArc(sketch, "E27.filletArc", {"start": v(0.67, 10.58) * mm, "mid": v(0.72, 10.5) * mm, "end": v(0.8, 10.47) * mm});
            skLineSegment(sketch, "E28.MirrorCS", {"start": v(1.4, 10.41) * mm, "end": v(1.1, 10.44) * mm});
            skArc(sketch, "E29.MirrorCS", {"start": v(1.54, 10.49) * mm, "mid": v(1.48, 10.43) * mm, "end": v(1.4, 10.41) * mm});
            skLineSegment(sketch, "E30.MirrorCS", {"start": v(2.4, 11.25) * mm, "end": v(2.01, 11.33) * mm});
            skLineSegment(sketch, "E31.MirrorCS", {"start": v(2.01, 11.33) * mm, "end": v(1.54, 10.49) * mm});
            skLineSegment(sketch, "E32.1.0", {"start": v(-2.4, 11.25) * mm, "end": v(-2.01, 11.33) * mm});
            skLineSegment(sketch, "E32.1.1", {"start": v(-2.01, 11.33) * mm, "end": v(-1.54, 10.49) * mm});
            skArc(sketch, "E32.1.2", {"start": v(-1.54, 10.49) * mm, "mid": v(-1.48, 10.43) * mm, "end": v(-1.4, 10.41) * mm});
            skLineSegment(sketch, "E32.1.3", {"start": v(-1.4, 10.41) * mm, "end": v(-1.1, 10.44) * mm});
            skLineSegment(sketch, "E32.1.4", {"start": v(-0.8, 10.47) * mm, "end": v(-1.1, 10.44) * mm});
            skArc(sketch, "E32.1.5", {"start": v(-0.67, 10.58) * mm, "mid": v(-0.72, 10.5) * mm, "end": v(-0.8, 10.47) * mm});
            skLineSegment(sketch, "E32.1.6", {"start": v(-0.39, 11.5) * mm, "end": v(-0.67, 10.58) * mm});
            skLineSegment(sketch, "E32.1.7", {"start": v(0, 11.5) * mm, "end": v(-0.39, 11.5) * mm});
            skLineSegment(sketch, "E32.2.0", {"start": v(-4.68, 10.5) * mm, "end": v(-4.32, 10.66) * mm});
            skLineSegment(sketch, "E32.2.1", {"start": v(-4.32, 10.66) * mm, "end": v(-3.7, 9.94) * mm});
            skArc(sketch, "E32.2.2", {"start": v(-3.7, 9.94) * mm, "mid": v(-3.62, 9.9) * mm, "end": v(-3.53, 9.9) * mm});
            skLineSegment(sketch, "E32.2.3", {"start": v(-3.53, 9.9) * mm, "end": v(-3.24, 9.99) * mm});
            skLineSegment(sketch, "E32.2.4", {"start": v(-2.96, 10.08) * mm, "end": v(-3.24, 9.99) * mm});
            skArc(sketch, "E32.2.5", {"start": v(-2.86, 10.2) * mm, "mid": v(-2.89, 10.13) * mm, "end": v(-2.96, 10.08) * mm});
            skLineSegment(sketch, "E32.2.6", {"start": v(-2.77, 11.17) * mm, "end": v(-2.86, 10.2) * mm});
            skLineSegment(sketch, "E32.2.7", {"start": v(-2.4, 11.25) * mm, "end": v(-2.77, 11.17) * mm});
            skLineSegment(sketch, "E32.3.0", {"start": v(-6.76, 9.3) * mm, "end": v(-6.45, 9.53) * mm});
            skLineSegment(sketch, "E32.3.1", {"start": v(-6.45, 9.53) * mm, "end": v(-5.68, 8.95) * mm});
            skArc(sketch, "E32.3.2", {"start": v(-5.68, 8.95) * mm, "mid": v(-5.6, 8.92) * mm, "end": v(-5.51, 8.94) * mm});
            skLineSegment(sketch, "E32.3.3", {"start": v(-5.51, 8.94) * mm, "end": v(-5.25, 9.1) * mm});
            skLineSegment(sketch, "E32.3.4", {"start": v(-4.99, 9.24) * mm, "end": v(-5.25, 9.1) * mm});
            skArc(sketch, "E32.3.5", {"start": v(-4.92, 9.4) * mm, "mid": v(-4.93, 9.3) * mm, "end": v(-4.99, 9.24) * mm});
            skLineSegment(sketch, "E32.3.6", {"start": v(-5.03, 10.35) * mm, "end": v(-4.92, 9.4) * mm});
            skLineSegment(sketch, "E32.3.7", {"start": v(-4.68, 10.5) * mm, "end": v(-5.03, 10.35) * mm});
            skLineSegment(sketch, "E32.4.0", {"start": v(-8.55, 7.7) * mm, "end": v(-8.29, 7.98) * mm});
            skLineSegment(sketch, "E32.4.1", {"start": v(-8.29, 7.98) * mm, "end": v(-7.41, 7.58) * mm});
            skArc(sketch, "E32.4.2", {"start": v(-7.41, 7.58) * mm, "mid": v(-7.33, 7.56) * mm, "end": v(-7.25, 7.6) * mm});
            skLineSegment(sketch, "E32.4.3", {"start": v(-7.25, 7.6) * mm, "end": v(-7.03, 7.8) * mm});
            skLineSegment(sketch, "E32.4.4", {"start": v(-6.8, 8) * mm, "end": v(-7.03, 7.8) * mm});
            skArc(sketch, "E32.4.5", {"start": v(-6.76, 8.16) * mm, "mid": v(-6.76, 8.08) * mm, "end": v(-6.8, 8) * mm});
            skLineSegment(sketch, "E32.4.6", {"start": v(-7.07, 9.08) * mm, "end": v(-6.76, 8.16) * mm});
            skLineSegment(sketch, "E32.4.7", {"start": v(-6.76, 9.3) * mm, "end": v(-7.07, 9.08) * mm});
            skLineSegment(sketch, "E32.5.0", {"start": v(-9.96, 5.75) * mm, "end": v(-9.77, 6.08) * mm});
            skLineSegment(sketch, "E32.5.1", {"start": v(-9.77, 6.08) * mm, "end": v(-8.83, 5.87) * mm});
            skArc(sketch, "E32.5.2", {"start": v(-8.83, 5.87) * mm, "mid": v(-8.74, 5.88) * mm, "end": v(-8.67, 5.93) * mm});
            skLineSegment(sketch, "E32.5.3", {"start": v(-8.67, 5.93) * mm, "end": v(-8.5, 6.17) * mm});
            skLineSegment(sketch, "E32.5.4", {"start": v(-8.32, 6.42) * mm, "end": v(-8.5, 6.17) * mm});
            skArc(sketch, "E32.5.5", {"start": v(-8.31, 6.58) * mm, "mid": v(-8.29, 6.5) * mm, "end": v(-8.32, 6.42) * mm});
            skLineSegment(sketch, "E32.5.6", {"start": v(-8.8, 7.4) * mm, "end": v(-8.31, 6.58) * mm});
            skLineSegment(sketch, "E32.5.7", {"start": v(-8.55, 7.7) * mm, "end": v(-8.8, 7.4) * mm});
            skLineSegment(sketch, "E32.6.0", {"start": v(-10.94, 3.55) * mm, "end": v(-10.82, 3.92) * mm});
            skLineSegment(sketch, "E32.6.1", {"start": v(-10.82, 3.92) * mm, "end": v(-9.85, 3.9) * mm});
            skArc(sketch, "E32.6.2", {"start": v(-9.85, 3.9) * mm, "mid": v(-9.77, 3.93) * mm, "end": v(-9.71, 4) * mm});
            skLineSegment(sketch, "E32.6.3", {"start": v(-9.71, 4) * mm, "end": v(-9.6, 4.27) * mm});
            skLineSegment(sketch, "E32.6.4", {"start": v(-9.47, 4.55) * mm, "end": v(-9.6, 4.27) * mm});
            skArc(sketch, "E32.6.5", {"start": v(-9.5, 4.7) * mm, "mid": v(-9.46, 4.63) * mm, "end": v(-9.47, 4.55) * mm});
            skLineSegment(sketch, "E32.6.6", {"start": v(-10.15, 5.42) * mm, "end": v(-9.5, 4.7) * mm});
            skLineSegment(sketch, "E32.6.7", {"start": v(-9.96, 5.75) * mm, "end": v(-10.15, 5.42) * mm});
            skLineSegment(sketch, "E32.7.0", {"start": v(-11.44, 1.2) * mm, "end": v(-11.4, 1.59) * mm});
            skLineSegment(sketch, "E32.7.1", {"start": v(-11.4, 1.59) * mm, "end": v(-10.45, 1.77) * mm});
            skArc(sketch, "E32.7.2", {"start": v(-10.45, 1.77) * mm, "mid": v(-10.37, 1.81) * mm, "end": v(-10.33, 1.89) * mm});
            skLineSegment(sketch, "E32.7.3", {"start": v(-10.33, 1.89) * mm, "end": v(-10.27, 2.18) * mm});
            skLineSegment(sketch, "E32.7.4", {"start": v(-10.2, 2.48) * mm, "end": v(-10.27, 2.18) * mm});
            skArc(sketch, "E32.7.5", {"start": v(-10.27, 2.63) * mm, "mid": v(-10.22, 2.56) * mm, "end": v(-10.2, 2.48) * mm});
            skLineSegment(sketch, "E32.7.6", {"start": v(-11.06, 3.19) * mm, "end": v(-10.27, 2.63) * mm});
            skLineSegment(sketch, "E32.7.7", {"start": v(-10.94, 3.55) * mm, "end": v(-11.06, 3.19) * mm});
            skLineSegment(sketch, "E32.8.0", {"start": v(-11.44, -1.2) * mm, "end": v(-11.48, -0.82) * mm});
            skLineSegment(sketch, "E32.8.1", {"start": v(-11.48, -0.82) * mm, "end": v(-10.6, -0.44) * mm});
            skArc(sketch, "E32.8.2", {"start": v(-10.6, -0.44) * mm, "mid": v(-10.52, -0.38) * mm, "end": v(-10.5, -0.3) * mm});
            skLineSegment(sketch, "E32.8.3", {"start": v(-10.5, -0.3) * mm, "end": v(-10.5, 0) * mm});
            skLineSegment(sketch, "E32.8.4", {"start": v(-10.5, 0.3) * mm, "end": v(-10.5, 0) * mm});
            skArc(sketch, "E32.8.5", {"start": v(-10.6, 0.44) * mm, "mid": v(-10.52, 0.38) * mm, "end": v(-10.5, 0.3) * mm});
            skLineSegment(sketch, "E32.8.6", {"start": v(-11.48, 0.82) * mm, "end": v(-10.6, 0.44) * mm});
            skLineSegment(sketch, "E32.8.7", {"start": v(-11.44, 1.2) * mm, "end": v(-11.48, 0.82) * mm});
            skLineSegment(sketch, "E32.9.0", {"start": v(-10.94, -3.55) * mm, "end": v(-11.06, -3.19) * mm});
            skLineSegment(sketch, "E32.9.1", {"start": v(-11.06, -3.19) * mm, "end": v(-10.27, -2.63) * mm});
            skArc(sketch, "E32.9.2", {"start": v(-10.27, -2.63) * mm, "mid": v(-10.22, -2.56) * mm, "end": v(-10.2, -2.48) * mm});
            skLineSegment(sketch, "E32.9.3", {"start": v(-10.2, -2.48) * mm, "end": v(-10.27, -2.18) * mm});
            skLineSegment(sketch, "E32.9.4", {"start": v(-10.33, -1.89) * mm, "end": v(-10.27, -2.18) * mm});
            skArc(sketch, "E32.9.5", {"start": v(-10.45, -1.77) * mm, "mid": v(-10.37, -1.81) * mm, "end": v(-10.33, -1.89) * mm});
            skLineSegment(sketch, "E32.9.6", {"start": v(-11.4, -1.59) * mm, "end": v(-10.45, -1.77) * mm});
            skLineSegment(sketch, "E32.9.7", {"start": v(-11.44, -1.2) * mm, "end": v(-11.4, -1.59) * mm});
            skLineSegment(sketch, "E32.10.0", {"start": v(-9.96, -5.75) * mm, "end": v(-10.15, -5.42) * mm});
            skLineSegment(sketch, "E32.10.1", {"start": v(-10.15, -5.42) * mm, "end": v(-9.5, -4.7) * mm});
            skArc(sketch, "E32.10.2", {"start": v(-9.5, -4.7) * mm, "mid": v(-9.46, -4.63) * mm, "end": v(-9.47, -4.55) * mm});
            skLineSegment(sketch, "E32.10.3", {"start": v(-9.47, -4.55) * mm, "end": v(-9.6, -4.27) * mm});
            skLineSegment(sketch, "E32.10.4", {"start": v(-9.71, -4) * mm, "end": v(-9.6, -4.27) * mm});
            skArc(sketch, "E32.10.5", {"start": v(-9.85, -3.9) * mm, "mid": v(-9.77, -3.93) * mm, "end": v(-9.71, -4) * mm});
            skLineSegment(sketch, "E32.10.6", {"start": v(-10.82, -3.92) * mm, "end": v(-9.85, -3.9) * mm});
            skLineSegment(sketch, "E32.10.7", {"start": v(-10.94, -3.55) * mm, "end": v(-10.82, -3.92) * mm});
            skLineSegment(sketch, "E32.11.0", {"start": v(-8.55, -7.7) * mm, "end": v(-8.8, -7.4) * mm});
            skLineSegment(sketch, "E32.11.1", {"start": v(-8.8, -7.4) * mm, "end": v(-8.31, -6.58) * mm});
            skArc(sketch, "E32.11.2", {"start": v(-8.31, -6.58) * mm, "mid": v(-8.29, -6.5) * mm, "end": v(-8.32, -6.42) * mm});
            skLineSegment(sketch, "E32.11.3", {"start": v(-8.32, -6.42) * mm, "end": v(-8.5, -6.17) * mm});
            skLineSegment(sketch, "E32.11.4", {"start": v(-8.67, -5.93) * mm, "end": v(-8.5, -6.17) * mm});
            skArc(sketch, "E32.11.5", {"start": v(-8.83, -5.87) * mm, "mid": v(-8.74, -5.88) * mm, "end": v(-8.67, -5.93) * mm});
            skLineSegment(sketch, "E32.11.6", {"start": v(-9.77, -6.08) * mm, "end": v(-8.83, -5.87) * mm});
            skLineSegment(sketch, "E32.11.7", {"start": v(-9.96, -5.75) * mm, "end": v(-9.77, -6.08) * mm});
            skLineSegment(sketch, "E32.12.0", {"start": v(-6.76, -9.3) * mm, "end": v(-7.07, -9.08) * mm});
            skLineSegment(sketch, "E32.12.1", {"start": v(-7.07, -9.08) * mm, "end": v(-6.76, -8.16) * mm});
            skArc(sketch, "E32.12.2", {"start": v(-6.76, -8.16) * mm, "mid": v(-6.76, -8.08) * mm, "end": v(-6.8, -8) * mm});
            skLineSegment(sketch, "E32.12.3", {"start": v(-6.8, -8) * mm, "end": v(-7.03, -7.8) * mm});
            skLineSegment(sketch, "E32.12.4", {"start": v(-7.25, -7.6) * mm, "end": v(-7.03, -7.8) * mm});
            skArc(sketch, "E32.12.5", {"start": v(-7.41, -7.58) * mm, "mid": v(-7.33, -7.56) * mm, "end": v(-7.25, -7.6) * mm});
            skLineSegment(sketch, "E32.12.6", {"start": v(-8.29, -7.98) * mm, "end": v(-7.41, -7.58) * mm});
            skLineSegment(sketch, "E32.12.7", {"start": v(-8.55, -7.7) * mm, "end": v(-8.29, -7.98) * mm});
            skLineSegment(sketch, "E32.13.0", {"start": v(-4.68, -10.5) * mm, "end": v(-5.03, -10.35) * mm});
            skLineSegment(sketch, "E32.13.1", {"start": v(-5.03, -10.35) * mm, "end": v(-4.92, -9.4) * mm});
            skArc(sketch, "E32.13.2", {"start": v(-4.92, -9.4) * mm, "mid": v(-4.93, -9.3) * mm, "end": v(-4.99, -9.24) * mm});
            skLineSegment(sketch, "E32.13.3", {"start": v(-4.99, -9.24) * mm, "end": v(-5.25, -9.1) * mm});
            skLineSegment(sketch, "E32.13.4", {"start": v(-5.51, -8.94) * mm, "end": v(-5.25, -9.1) * mm});
            skArc(sketch, "E32.13.5", {"start": v(-5.68, -8.95) * mm, "mid": v(-5.6, -8.92) * mm, "end": v(-5.51, -8.94) * mm});
            skLineSegment(sketch, "E32.13.6", {"start": v(-6.45, -9.53) * mm, "end": v(-5.68, -8.95) * mm});
            skLineSegment(sketch, "E32.13.7", {"start": v(-6.76, -9.3) * mm, "end": v(-6.45, -9.53) * mm});
            skLineSegment(sketch, "E32.14.0", {"start": v(-2.4, -11.25) * mm, "end": v(-2.77, -11.17) * mm});
            skLineSegment(sketch, "E32.14.1", {"start": v(-2.77, -11.17) * mm, "end": v(-2.86, -10.2) * mm});
            skArc(sketch, "E32.14.2", {"start": v(-2.86, -10.2) * mm, "mid": v(-2.89, -10.13) * mm, "end": v(-2.96, -10.08) * mm});
            skLineSegment(sketch, "E32.14.3", {"start": v(-2.96, -10.08) * mm, "end": v(-3.24, -9.99) * mm});
            skLineSegment(sketch, "E32.14.4", {"start": v(-3.53, -9.9) * mm, "end": v(-3.24, -9.99) * mm});
            skArc(sketch, "E32.14.5", {"start": v(-3.7, -9.94) * mm, "mid": v(-3.62, -9.9) * mm, "end": v(-3.53, -9.9) * mm});
            skLineSegment(sketch, "E32.14.6", {"start": v(-4.32, -10.66) * mm, "end": v(-3.7, -9.94) * mm});
            skLineSegment(sketch, "E32.14.7", {"start": v(-4.68, -10.5) * mm, "end": v(-4.32, -10.66) * mm});
            skLineSegment(sketch, "E32.15.0", {"start": v(0, -11.5) * mm, "end": v(-0.39, -11.5) * mm});
            skLineSegment(sketch, "E32.15.1", {"start": v(-0.39, -11.5) * mm, "end": v(-0.67, -10.58) * mm});
            skArc(sketch, "E32.15.2", {"start": v(-0.67, -10.58) * mm, "mid": v(-0.72, -10.5) * mm, "end": v(-0.8, -10.47) * mm});
            skLineSegment(sketch, "E32.15.3", {"start": v(-0.8, -10.47) * mm, "end": v(-1.1, -10.44) * mm});
            skLineSegment(sketch, "E32.15.4", {"start": v(-1.4, -10.41) * mm, "end": v(-1.1, -10.44) * mm});
            skArc(sketch, "E32.15.5", {"start": v(-1.54, -10.49) * mm, "mid": v(-1.48, -10.43) * mm, "end": v(-1.4, -10.41) * mm});
            skLineSegment(sketch, "E32.15.6", {"start": v(-2.01, -11.33) * mm, "end": v(-1.54, -10.49) * mm});
            skLineSegment(sketch, "E32.15.7", {"start": v(-2.4, -11.25) * mm, "end": v(-2.01, -11.33) * mm});
            skLineSegment(sketch, "E32.16.0", {"start": v(2.4, -11.25) * mm, "end": v(2.01, -11.33) * mm});
            skLineSegment(sketch, "E32.16.1", {"start": v(2.01, -11.33) * mm, "end": v(1.54, -10.49) * mm});
            skArc(sketch, "E32.16.2", {"start": v(1.54, -10.49) * mm, "mid": v(1.48, -10.43) * mm, "end": v(1.4, -10.41) * mm});
            skLineSegment(sketch, "E32.16.3", {"start": v(1.4, -10.41) * mm, "end": v(1.1, -10.44) * mm});
            skLineSegment(sketch, "E32.16.4", {"start": v(0.8, -10.47) * mm, "end": v(1.1, -10.44) * mm});
            skArc(sketch, "E32.16.5", {"start": v(0.67, -10.58) * mm, "mid": v(0.72, -10.5) * mm, "end": v(0.8, -10.47) * mm});
            skLineSegment(sketch, "E32.16.6", {"start": v(0.39, -11.5) * mm, "end": v(0.67, -10.58) * mm});
            skLineSegment(sketch, "E32.16.7", {"start": v(0, -11.5) * mm, "end": v(0.39, -11.5) * mm});
            skLineSegment(sketch, "E32.17.0", {"start": v(4.68, -10.5) * mm, "end": v(4.32, -10.66) * mm});
            skLineSegment(sketch, "E32.17.1", {"start": v(4.32, -10.66) * mm, "end": v(3.7, -9.94) * mm});
            skArc(sketch, "E32.17.2", {"start": v(3.7, -9.94) * mm, "mid": v(3.62, -9.9) * mm, "end": v(3.53, -9.9) * mm});
            skLineSegment(sketch, "E32.17.3", {"start": v(3.53, -9.9) * mm, "end": v(3.24, -9.99) * mm});
            skLineSegment(sketch, "E32.17.4", {"start": v(2.96, -10.08) * mm, "end": v(3.24, -9.99) * mm});
            skArc(sketch, "E32.17.5", {"start": v(2.86, -10.2) * mm, "mid": v(2.89, -10.13) * mm, "end": v(2.96, -10.08) * mm});
            skLineSegment(sketch, "E32.17.6", {"start": v(2.77, -11.17) * mm, "end": v(2.86, -10.2) * mm});
            skLineSegment(sketch, "E32.17.7", {"start": v(2.4, -11.25) * mm, "end": v(2.77, -11.17) * mm});
            skLineSegment(sketch, "E32.18.0", {"start": v(6.76, -9.3) * mm, "end": v(6.45, -9.53) * mm});
            skLineSegment(sketch, "E32.18.1", {"start": v(6.45, -9.53) * mm, "end": v(5.68, -8.95) * mm});
            skArc(sketch, "E32.18.2", {"start": v(5.68, -8.95) * mm, "mid": v(5.6, -8.92) * mm, "end": v(5.51, -8.94) * mm});
            skLineSegment(sketch, "E32.18.3", {"start": v(5.51, -8.94) * mm, "end": v(5.25, -9.1) * mm});
            skLineSegment(sketch, "E32.18.4", {"start": v(4.99, -9.24) * mm, "end": v(5.25, -9.1) * mm});
            skArc(sketch, "E32.18.5", {"start": v(4.92, -9.4) * mm, "mid": v(4.93, -9.3) * mm, "end": v(4.99, -9.24) * mm});
            skLineSegment(sketch, "E32.18.6", {"start": v(5.03, -10.35) * mm, "end": v(4.92, -9.4) * mm});
            skLineSegment(sketch, "E32.18.7", {"start": v(4.68, -10.5) * mm, "end": v(5.03, -10.35) * mm});
            skLineSegment(sketch, "E32.19.0", {"start": v(8.55, -7.7) * mm, "end": v(8.29, -7.98) * mm});
            skLineSegment(sketch, "E32.19.1", {"start": v(8.29, -7.98) * mm, "end": v(7.41, -7.58) * mm});
            skArc(sketch, "E32.19.2", {"start": v(7.41, -7.58) * mm, "mid": v(7.33, -7.56) * mm, "end": v(7.25, -7.6) * mm});
            skLineSegment(sketch, "E32.19.3", {"start": v(7.25, -7.6) * mm, "end": v(7.03, -7.8) * mm});
            skLineSegment(sketch, "E32.19.4", {"start": v(6.8, -8) * mm, "end": v(7.03, -7.8) * mm});
            skArc(sketch, "E32.19.5", {"start": v(6.76, -8.16) * mm, "mid": v(6.76, -8.08) * mm, "end": v(6.8, -8) * mm});
            skLineSegment(sketch, "E32.19.6", {"start": v(7.07, -9.08) * mm, "end": v(6.76, -8.16) * mm});
            skLineSegment(sketch, "E32.19.7", {"start": v(6.76, -9.3) * mm, "end": v(7.07, -9.08) * mm});
            skLineSegment(sketch, "E32.20.0", {"start": v(9.96, -5.75) * mm, "end": v(9.77, -6.08) * mm});
            skLineSegment(sketch, "E32.20.1", {"start": v(9.77, -6.08) * mm, "end": v(8.83, -5.87) * mm});
            skArc(sketch, "E32.20.2", {"start": v(8.83, -5.87) * mm, "mid": v(8.74, -5.88) * mm, "end": v(8.67, -5.93) * mm});
            skLineSegment(sketch, "E32.20.3", {"start": v(8.67, -5.93) * mm, "end": v(8.5, -6.17) * mm});
            skLineSegment(sketch, "E32.20.4", {"start": v(8.32, -6.42) * mm, "end": v(8.5, -6.17) * mm});
            skArc(sketch, "E32.20.5", {"start": v(8.31, -6.58) * mm, "mid": v(8.29, -6.5) * mm, "end": v(8.32, -6.42) * mm});
            skLineSegment(sketch, "E32.20.6", {"start": v(8.8, -7.4) * mm, "end": v(8.31, -6.58) * mm});
            skLineSegment(sketch, "E32.20.7", {"start": v(8.55, -7.7) * mm, "end": v(8.8, -7.4) * mm});
            skLineSegment(sketch, "E32.21.0", {"start": v(10.94, -3.55) * mm, "end": v(10.82, -3.92) * mm});
            skLineSegment(sketch, "E32.21.1", {"start": v(10.82, -3.92) * mm, "end": v(9.85, -3.9) * mm});
            skArc(sketch, "E32.21.2", {"start": v(9.85, -3.9) * mm, "mid": v(9.77, -3.93) * mm, "end": v(9.71, -4) * mm});
            skLineSegment(sketch, "E32.21.3", {"start": v(9.71, -4) * mm, "end": v(9.6, -4.27) * mm});
            skLineSegment(sketch, "E32.21.4", {"start": v(9.47, -4.55) * mm, "end": v(9.6, -4.27) * mm});
            skArc(sketch, "E32.21.5", {"start": v(9.5, -4.7) * mm, "mid": v(9.46, -4.63) * mm, "end": v(9.47, -4.55) * mm});
            skLineSegment(sketch, "E32.21.6", {"start": v(10.15, -5.42) * mm, "end": v(9.5, -4.7) * mm});
            skLineSegment(sketch, "E32.21.7", {"start": v(9.96, -5.75) * mm, "end": v(10.15, -5.42) * mm});
            skLineSegment(sketch, "E32.22.0", {"start": v(11.44, -1.2) * mm, "end": v(11.4, -1.59) * mm});
            skLineSegment(sketch, "E32.22.1", {"start": v(11.4, -1.59) * mm, "end": v(10.45, -1.77) * mm});
            skArc(sketch, "E32.22.2", {"start": v(10.45, -1.77) * mm, "mid": v(10.37, -1.81) * mm, "end": v(10.33, -1.89) * mm});
            skLineSegment(sketch, "E32.22.3", {"start": v(10.33, -1.89) * mm, "end": v(10.27, -2.18) * mm});
            skLineSegment(sketch, "E32.22.4", {"start": v(10.2, -2.48) * mm, "end": v(10.27, -2.18) * mm});
            skArc(sketch, "E32.22.5", {"start": v(10.27, -2.63) * mm, "mid": v(10.22, -2.56) * mm, "end": v(10.2, -2.48) * mm});
            skLineSegment(sketch, "E32.22.6", {"start": v(11.06, -3.19) * mm, "end": v(10.27, -2.63) * mm});
            skLineSegment(sketch, "E32.22.7", {"start": v(10.94, -3.55) * mm, "end": v(11.06, -3.19) * mm});
            skLineSegment(sketch, "E32.23.0", {"start": v(11.44, 1.2) * mm, "end": v(11.48, 0.82) * mm});
            skLineSegment(sketch, "E32.23.1", {"start": v(11.48, 0.82) * mm, "end": v(10.6, 0.44) * mm});
            skArc(sketch, "E32.23.2", {"start": v(10.6, 0.44) * mm, "mid": v(10.52, 0.38) * mm, "end": v(10.5, 0.3) * mm});
            skLineSegment(sketch, "E32.23.3", {"start": v(10.5, 0.3) * mm, "end": v(10.5, 0) * mm});
            skLineSegment(sketch, "E32.23.4", {"start": v(10.5, -0.3) * mm, "end": v(10.5, 0) * mm});
            skArc(sketch, "E32.23.5", {"start": v(10.6, -0.44) * mm, "mid": v(10.52, -0.38) * mm, "end": v(10.5, -0.3) * mm});
            skLineSegment(sketch, "E32.23.6", {"start": v(11.48, -0.82) * mm, "end": v(10.6, -0.44) * mm});
            skLineSegment(sketch, "E32.23.7", {"start": v(11.44, -1.2) * mm, "end": v(11.48, -0.82) * mm});
            skLineSegment(sketch, "E32.24.0", {"start": v(10.94, 3.55) * mm, "end": v(11.06, 3.19) * mm});
            skLineSegment(sketch, "E32.24.1", {"start": v(11.06, 3.19) * mm, "end": v(10.27, 2.63) * mm});
            skArc(sketch, "E32.24.2", {"start": v(10.27, 2.63) * mm, "mid": v(10.22, 2.56) * mm, "end": v(10.2, 2.48) * mm});
            skLineSegment(sketch, "E32.24.3", {"start": v(10.2, 2.48) * mm, "end": v(10.27, 2.18) * mm});
            skLineSegment(sketch, "E32.24.4", {"start": v(10.33, 1.89) * mm, "end": v(10.27, 2.18) * mm});
            skArc(sketch, "E32.24.5", {"start": v(10.45, 1.77) * mm, "mid": v(10.37, 1.81) * mm, "end": v(10.33, 1.89) * mm});
            skLineSegment(sketch, "E32.24.6", {"start": v(11.4, 1.59) * mm, "end": v(10.45, 1.77) * mm});
            skLineSegment(sketch, "E32.24.7", {"start": v(11.44, 1.2) * mm, "end": v(11.4, 1.59) * mm});
            skLineSegment(sketch, "E32.25.0", {"start": v(9.96, 5.75) * mm, "end": v(10.15, 5.42) * mm});
            skLineSegment(sketch, "E32.25.1", {"start": v(10.15, 5.42) * mm, "end": v(9.5, 4.7) * mm});
            skArc(sketch, "E32.25.2", {"start": v(9.5, 4.7) * mm, "mid": v(9.46, 4.63) * mm, "end": v(9.47, 4.55) * mm});
            skLineSegment(sketch, "E32.25.3", {"start": v(9.47, 4.55) * mm, "end": v(9.6, 4.27) * mm});
            skLineSegment(sketch, "E32.25.4", {"start": v(9.71, 4) * mm, "end": v(9.6, 4.27) * mm});
            skArc(sketch, "E32.25.5", {"start": v(9.85, 3.9) * mm, "mid": v(9.77, 3.93) * mm, "end": v(9.71, 4) * mm});
            skLineSegment(sketch, "E32.25.6", {"start": v(10.82, 3.92) * mm, "end": v(9.85, 3.9) * mm});
            skLineSegment(sketch, "E32.25.7", {"start": v(10.94, 3.55) * mm, "end": v(10.82, 3.92) * mm});
            skLineSegment(sketch, "E32.26.0", {"start": v(8.55, 7.7) * mm, "end": v(8.8, 7.4) * mm});
            skLineSegment(sketch, "E32.26.1", {"start": v(8.8, 7.4) * mm, "end": v(8.31, 6.58) * mm});
            skArc(sketch, "E32.26.2", {"start": v(8.31, 6.58) * mm, "mid": v(8.29, 6.5) * mm, "end": v(8.32, 6.42) * mm});
            skLineSegment(sketch, "E32.26.3", {"start": v(8.32, 6.42) * mm, "end": v(8.5, 6.17) * mm});
            skLineSegment(sketch, "E32.26.4", {"start": v(8.67, 5.93) * mm, "end": v(8.5, 6.17) * mm});
            skArc(sketch, "E32.26.5", {"start": v(8.83, 5.87) * mm, "mid": v(8.74, 5.88) * mm, "end": v(8.67, 5.93) * mm});
            skLineSegment(sketch, "E32.26.6", {"start": v(9.77, 6.08) * mm, "end": v(8.83, 5.87) * mm});
            skLineSegment(sketch, "E32.26.7", {"start": v(9.96, 5.75) * mm, "end": v(9.77, 6.08) * mm});
            skLineSegment(sketch, "E32.27.0", {"start": v(6.76, 9.3) * mm, "end": v(7.07, 9.08) * mm});
            skLineSegment(sketch, "E32.27.1", {"start": v(7.07, 9.08) * mm, "end": v(6.76, 8.16) * mm});
            skArc(sketch, "E32.27.2", {"start": v(6.76, 8.16) * mm, "mid": v(6.76, 8.08) * mm, "end": v(6.8, 8) * mm});
            skLineSegment(sketch, "E32.27.3", {"start": v(6.8, 8) * mm, "end": v(7.03, 7.8) * mm});
            skLineSegment(sketch, "E32.27.4", {"start": v(7.25, 7.6) * mm, "end": v(7.03, 7.8) * mm});
            skArc(sketch, "E32.27.5", {"start": v(7.41, 7.58) * mm, "mid": v(7.33, 7.56) * mm, "end": v(7.25, 7.6) * mm});
            skLineSegment(sketch, "E32.27.6", {"start": v(8.29, 7.98) * mm, "end": v(7.41, 7.58) * mm});
            skLineSegment(sketch, "E32.27.7", {"start": v(8.55, 7.7) * mm, "end": v(8.29, 7.98) * mm});
            skLineSegment(sketch, "E32.28.0", {"start": v(4.68, 10.5) * mm, "end": v(5.03, 10.35) * mm});
            skLineSegment(sketch, "E32.28.1", {"start": v(5.03, 10.35) * mm, "end": v(4.92, 9.4) * mm});
            skArc(sketch, "E32.28.2", {"start": v(4.92, 9.4) * mm, "mid": v(4.93, 9.3) * mm, "end": v(4.99, 9.24) * mm});
            skLineSegment(sketch, "E32.28.3", {"start": v(4.99, 9.24) * mm, "end": v(5.25, 9.1) * mm});
            skLineSegment(sketch, "E32.28.4", {"start": v(5.51, 8.94) * mm, "end": v(5.25, 9.1) * mm});
            skArc(sketch, "E32.28.5", {"start": v(5.68, 8.95) * mm, "mid": v(5.6, 8.92) * mm, "end": v(5.51, 8.94) * mm});
            skLineSegment(sketch, "E32.28.6", {"start": v(6.45, 9.53) * mm, "end": v(5.68, 8.95) * mm});
            skLineSegment(sketch, "E32.28.7", {"start": v(6.76, 9.3) * mm, "end": v(6.45, 9.53) * mm});
            skLineSegment(sketch, "E32.29.0", {"start": v(2.4, 11.25) * mm, "end": v(2.77, 11.17) * mm});
            skLineSegment(sketch, "E32.29.1", {"start": v(2.77, 11.17) * mm, "end": v(2.86, 10.2) * mm});
            skArc(sketch, "E32.29.2", {"start": v(2.86, 10.2) * mm, "mid": v(2.89, 10.13) * mm, "end": v(2.96, 10.08) * mm});
            skLineSegment(sketch, "E32.29.3", {"start": v(2.96, 10.08) * mm, "end": v(3.24, 9.99) * mm});
            skLineSegment(sketch, "E32.29.4", {"start": v(3.53, 9.9) * mm, "end": v(3.24, 9.99) * mm});
            skArc(sketch, "E32.29.5", {"start": v(3.7, 9.94) * mm, "mid": v(3.62, 9.9) * mm, "end": v(3.53, 9.9) * mm});
            skLineSegment(sketch, "E32.29.6", {"start": v(4.32, 10.66) * mm, "end": v(3.7, 9.94) * mm});
            skLineSegment(sketch, "E32.29.7", {"start": v(4.68, 10.5) * mm, "end": v(4.32, 10.66) * mm});
            skPoint(sketch, "E32.center", {"position": v(0, 0) * mm});
            skSolve(sketch);
        }
        {
            var Q0;
            Q0=qCreatedBy(makeId("Top.planeOp"),FACE);
            var sketch = newSketch(context, id + "F14", { "sketchPlane" : qUnion([Q0])});
            skCircle(sketch, "E33", {"center": v(0, 0) * mm, "radius": 12.5 * mm});
            skSolve(sketch);
        }
        {
            var Q0;
            Q0=qSketchRegion(id+"F14",true);
            extrude(context, id + "F15", {"entities" : qUnion([Q0]), "depth" : (getVariable(context, 'THICK')) * mm});
        }
        {
            var Q0;
            Q0=qSketchRegion(id+"F13",true);
            extrude(context, id + "F16", {"entities" : qUnion([Q0]), "operationType" : NewBodyOperationType.REMOVE, "depth" : 25 * mm});
        }
        {
            var Q0;
            Q0=qCreatedBy(makeId("Front.planeOp"),FACE);
            var sketch = newSketch(context, id + "F17", { "sketchPlane" : qUnion([Q0])});
            skLineSegment(sketch, "E34", {"start": v(0, 0) * mm, "end": v(0, 5.62) * mm});
            skSolve(sketch);
        }
        {
            var Q0;
            Q0=makeQuery(id+"F15.opExtrude","SWEPT_BODY",BODY,{"disambiguationData":[OSD([sQuery(id+"F14.wireOp",EDGE,"E33")])]});
            var Q1;
            Q1=sQuery(id+"F17.wireOp",EDGE,"E34");
            transform(context, id + "F18", {"entities" : qUnion([Q0]), "transformType" : TransformType.ROTATION, "transformAxis" : qUnion([Q1]), "angle" : 0 * degree, "makeCopy" : false});
        }
        {
            var Q0;
            Q0=qCreatedBy(makeId("Top.planeOp"),FACE);
            var sketch = newSketch(context, id + "F19", { "sketchPlane" : qUnion([Q0])});
            skCircle(sketch, "E35.cCircle", {"center": v(0, 0) * mm, "radius": 3.5 * mm, "construction": true});
            skLineSegment(sketch, "E35.0", {"start": v(-3.5, -6.06) * mm, "end": v(-3.5, 6.06) * mm});
            skLineSegment(sketch, "E35.1", {"start": v(-3.5, 6.06) * mm, "end": v(7, 0) * mm});
            skLineSegment(sketch, "E35.2", {"start": v(7, 0) * mm, "end": v(-3.5, -6.06) * mm});
            skPoint(sketch, "E35.0.midPoint", {"position": v(-3.5, 0) * mm});
            skLineSegment(sketch, "E36", {"start": v(0, 0) * mm, "end": v(7, 0) * mm});
            skLineSegment(sketch, "E37", {"start": v(0, 0) * mm, "end": v(-3.5, 6.06) * mm});
            skLineSegment(sketch, "E38", {"start": v(0, 0) * mm, "end": v(-3.5, -6.06) * mm});
            skSolve(sketch);
        }
        {
            var Q0;
            Q0=makeQuery(id+"F3.opExtrude","SWEPT_BODY",BODY,{"disambiguationData":[OSD([sQuery(id+"F2.wireOp",EDGE,"E6"),sQuery(id+"F2.wireOp",EDGE,"E7"),sQuery(id+"F2.wireOp",EDGE,"E8"),sQuery(id+"F2.wireOp",EDGE,"E9.filletArc"),sQuery(id+"F2.wireOp",EDGE,"E10.MirrorCS"),sQuery(id+"F2.wireOp",EDGE,"E11.MirrorCS"),sQuery(id+"F2.wireOp",EDGE,"E12.MirrorCS"),sQuery(id+"F2.wireOp",EDGE,"E13.MirrorCS"),sQuery(id+"F2.wireOp",EDGE,"E14.1.0"),sQuery(id+"F2.wireOp",EDGE,"E14.1.1"),sQuery(id+"F2.wireOp",EDGE,"E14.1.2"),sQuery(id+"F2.wireOp",EDGE,"E14.1.3"),sQuery(id+"F2.wireOp",EDGE,"E14.1.4"),sQuery(id+"F2.wireOp",EDGE,"E14.1.5"),sQuery(id+"F2.wireOp",EDGE,"E14.1.6"),sQuery(id+"F2.wireOp",EDGE,"E14.1.7"),sQuery(id+"F2.wireOp",EDGE,"E14.2.0"),sQuery(id+"F2.wireOp",EDGE,"E14.2.1"),sQuery(id+"F2.wireOp",EDGE,"E14.2.2"),sQuery(id+"F2.wireOp",EDGE,"E14.2.3"),sQuery(id+"F2.wireOp",EDGE,"E14.2.4"),sQuery(id+"F2.wireOp",EDGE,"E14.2.5"),sQuery(id+"F2.wireOp",EDGE,"E14.2.6"),sQuery(id+"F2.wireOp",EDGE,"E14.2.7"),sQuery(id+"F2.wireOp",EDGE,"E14.3.0"),sQuery(id+"F2.wireOp",EDGE,"E14.3.1"),sQuery(id+"F2.wireOp",EDGE,"E14.3.2"),sQuery(id+"F2.wireOp",EDGE,"E14.3.3"),sQuery(id+"F2.wireOp",EDGE,"E14.3.4"),sQuery(id+"F2.wireOp",EDGE,"E14.3.5"),sQuery(id+"F2.wireOp",EDGE,"E14.3.6"),sQuery(id+"F2.wireOp",EDGE,"E14.3.7"),sQuery(id+"F2.wireOp",EDGE,"E14.4.0"),sQuery(id+"F2.wireOp",EDGE,"E14.4.1"),sQuery(id+"F2.wireOp",EDGE,"E14.4.2"),sQuery(id+"F2.wireOp",EDGE,"E14.4.3"),sQuery(id+"F2.wireOp",EDGE,"E14.4.4"),sQuery(id+"F2.wireOp",EDGE,"E14.4.5"),sQuery(id+"F2.wireOp",EDGE,"E14.4.6"),sQuery(id+"F2.wireOp",EDGE,"E14.4.7"),sQuery(id+"F2.wireOp",EDGE,"E14.5.0"),sQuery(id+"F2.wireOp",EDGE,"E14.5.1"),sQuery(id+"F2.wireOp",EDGE,"E14.5.2"),sQuery(id+"F2.wireOp",EDGE,"E14.5.3"),sQuery(id+"F2.wireOp",EDGE,"E14.5.4"),sQuery(id+"F2.wireOp",EDGE,"E14.5.5"),sQuery(id+"F2.wireOp",EDGE,"E14.5.6"),sQuery(id+"F2.wireOp",EDGE,"E14.5.7"),sQuery(id+"F2.wireOp",EDGE,"E14.6.0"),sQuery(id+"F2.wireOp",EDGE,"E14.6.1"),sQuery(id+"F2.wireOp",EDGE,"E14.6.2"),sQuery(id+"F2.wireOp",EDGE,"E14.6.3"),sQuery(id+"F2.wireOp",EDGE,"E14.6.4"),sQuery(id+"F2.wireOp",EDGE,"E14.6.5"),sQuery(id+"F2.wireOp",EDGE,"E14.6.6"),sQuery(id+"F2.wireOp",EDGE,"E14.6.7"),sQuery(id+"F2.wireOp",EDGE,"E14.7.0"),sQuery(id+"F2.wireOp",EDGE,"E14.7.1"),sQuery(id+"F2.wireOp",EDGE,"E14.7.2"),sQuery(id+"F2.wireOp",EDGE,"E14.7.3"),sQuery(id+"F2.wireOp",EDGE,"E14.7.4"),sQuery(id+"F2.wireOp",EDGE,"E14.7.5"),sQuery(id+"F2.wireOp",EDGE,"E14.7.6"),sQuery(id+"F2.wireOp",EDGE,"E14.7.7"),sQuery(id+"F2.wireOp",EDGE,"E14.8.0"),sQuery(id+"F2.wireOp",EDGE,"E14.8.1"),sQuery(id+"F2.wireOp",EDGE,"E14.8.2"),sQuery(id+"F2.wireOp",EDGE,"E14.8.3"),sQuery(id+"F2.wireOp",EDGE,"E14.8.4"),sQuery(id+"F2.wireOp",EDGE,"E14.8.5"),sQuery(id+"F2.wireOp",EDGE,"E14.8.6"),sQuery(id+"F2.wireOp",EDGE,"E14.8.7"),sQuery(id+"F2.wireOp",EDGE,"E14.9.0"),sQuery(id+"F2.wireOp",EDGE,"E14.9.1"),sQuery(id+"F2.wireOp",EDGE,"E14.9.2"),sQuery(id+"F2.wireOp",EDGE,"E14.9.3"),sQuery(id+"F2.wireOp",EDGE,"E14.9.4"),sQuery(id+"F2.wireOp",EDGE,"E14.9.5"),sQuery(id+"F2.wireOp",EDGE,"E14.9.6"),sQuery(id+"F2.wireOp",EDGE,"E14.9.7")])]});
            var Q1;
            Q1=sQuery(id+"F17.wireOp",EDGE,"E34");
            transform(context, id + "F20", {"entities" : qUnion([Q0]), "transformType" : TransformType.ROTATION, "transformAxis" : qUnion([Q1]), "angle" : 0 * degree, "makeCopy" : false});
        }
        {
            var Q0;
            Q0=makeQuery(id+"F6.opPattern","COPY",BODY,{"derivedFrom":makeQuery(id+"F3.opExtrude","SWEPT_BODY",BODY,{"disambiguationData":[OSD([sQuery(id+"F2.wireOp",EDGE,"E6"),sQuery(id+"F2.wireOp",EDGE,"E7"),sQuery(id+"F2.wireOp",EDGE,"E8"),sQuery(id+"F2.wireOp",EDGE,"E9.filletArc"),sQuery(id+"F2.wireOp",EDGE,"E10.MirrorCS"),sQuery(id+"F2.wireOp",EDGE,"E11.MirrorCS"),sQuery(id+"F2.wireOp",EDGE,"E12.MirrorCS"),sQuery(id+"F2.wireOp",EDGE,"E13.MirrorCS"),sQuery(id+"F2.wireOp",EDGE,"E14.1.0"),sQuery(id+"F2.wireOp",EDGE,"E14.1.1"),sQuery(id+"F2.wireOp",EDGE,"E14.1.2"),sQuery(id+"F2.wireOp",EDGE,"E14.1.3"),sQuery(id+"F2.wireOp",EDGE,"E14.1.4"),sQuery(id+"F2.wireOp",EDGE,"E14.1.5"),sQuery(id+"F2.wireOp",EDGE,"E14.1.6"),sQuery(id+"F2.wireOp",EDGE,"E14.1.7"),sQuery(id+"F2.wireOp",EDGE,"E14.2.0"),sQuery(id+"F2.wireOp",EDGE,"E14.2.1"),sQuery(id+"F2.wireOp",EDGE,"E14.2.2"),sQuery(id+"F2.wireOp",EDGE,"E14.2.3"),sQuery(id+"F2.wireOp",EDGE,"E14.2.4"),sQuery(id+"F2.wireOp",EDGE,"E14.2.5"),sQuery(id+"F2.wireOp",EDGE,"E14.2.6"),sQuery(id+"F2.wireOp",EDGE,"E14.2.7"),sQuery(id+"F2.wireOp",EDGE,"E14.3.0"),sQuery(id+"F2.wireOp",EDGE,"E14.3.1"),sQuery(id+"F2.wireOp",EDGE,"E14.3.2"),sQuery(id+"F2.wireOp",EDGE,"E14.3.3"),sQuery(id+"F2.wireOp",EDGE,"E14.3.4"),sQuery(id+"F2.wireOp",EDGE,"E14.3.5"),sQuery(id+"F2.wireOp",EDGE,"E14.3.6"),sQuery(id+"F2.wireOp",EDGE,"E14.3.7"),sQuery(id+"F2.wireOp",EDGE,"E14.4.0"),sQuery(id+"F2.wireOp",EDGE,"E14.4.1"),sQuery(id+"F2.wireOp",EDGE,"E14.4.2"),sQuery(id+"F2.wireOp",EDGE,"E14.4.3"),sQuery(id+"F2.wireOp",EDGE,"E14.4.4"),sQuery(id+"F2.wireOp",EDGE,"E14.4.5"),sQuery(id+"F2.wireOp",EDGE,"E14.4.6"),sQuery(id+"F2.wireOp",EDGE,"E14.4.7"),sQuery(id+"F2.wireOp",EDGE,"E14.5.0"),sQuery(id+"F2.wireOp",EDGE,"E14.5.1"),sQuery(id+"F2.wireOp",EDGE,"E14.5.2"),sQuery(id+"F2.wireOp",EDGE,"E14.5.3"),sQuery(id+"F2.wireOp",EDGE,"E14.5.4"),sQuery(id+"F2.wireOp",EDGE,"E14.5.5"),sQuery(id+"F2.wireOp",EDGE,"E14.5.6"),sQuery(id+"F2.wireOp",EDGE,"E14.5.7"),sQuery(id+"F2.wireOp",EDGE,"E14.6.0"),sQuery(id+"F2.wireOp",EDGE,"E14.6.1"),sQuery(id+"F2.wireOp",EDGE,"E14.6.2"),sQuery(id+"F2.wireOp",EDGE,"E14.6.3"),sQuery(id+"F2.wireOp",EDGE,"E14.6.4"),sQuery(id+"F2.wireOp",EDGE,"E14.6.5"),sQuery(id+"F2.wireOp",EDGE,"E14.6.6"),sQuery(id+"F2.wireOp",EDGE,"E14.6.7"),sQuery(id+"F2.wireOp",EDGE,"E14.7.0"),sQuery(id+"F2.wireOp",EDGE,"E14.7.1"),sQuery(id+"F2.wireOp",EDGE,"E14.7.2"),sQuery(id+"F2.wireOp",EDGE,"E14.7.3"),sQuery(id+"F2.wireOp",EDGE,"E14.7.4"),sQuery(id+"F2.wireOp",EDGE,"E14.7.5"),sQuery(id+"F2.wireOp",EDGE,"E14.7.6"),sQuery(id+"F2.wireOp",EDGE,"E14.7.7"),sQuery(id+"F2.wireOp",EDGE,"E14.8.0"),sQuery(id+"F2.wireOp",EDGE,"E14.8.1"),sQuery(id+"F2.wireOp",EDGE,"E14.8.2"),sQuery(id+"F2.wireOp",EDGE,"E14.8.3"),sQuery(id+"F2.wireOp",EDGE,"E14.8.4"),sQuery(id+"F2.wireOp",EDGE,"E14.8.5"),sQuery(id+"F2.wireOp",EDGE,"E14.8.6"),sQuery(id+"F2.wireOp",EDGE,"E14.8.7"),sQuery(id+"F2.wireOp",EDGE,"E14.9.0"),sQuery(id+"F2.wireOp",EDGE,"E14.9.1"),sQuery(id+"F2.wireOp",EDGE,"E14.9.2"),sQuery(id+"F2.wireOp",EDGE,"E14.9.3"),sQuery(id+"F2.wireOp",EDGE,"E14.9.4"),sQuery(id+"F2.wireOp",EDGE,"E14.9.5"),sQuery(id+"F2.wireOp",EDGE,"E14.9.6"),sQuery(id+"F2.wireOp",EDGE,"E14.9.7")])]}),"instanceName":"1"});
            var Q1;
            Q1=sQuery(id+"F17.wireOp",EDGE,"E34");
            transform(context, id + "F21", {"entities" : qUnion([Q0]), "transformType" : TransformType.ROTATION, "transformAxis" : qUnion([Q1]), "angle" : 12 * degree, "makeCopy" : false});
        }
        {
            var Q0;
            Q0=makeQuery(id+"F11.opPattern","COPY",BODY,{"derivedFrom":makeQuery(id+"F6.opPattern","COPY",BODY,{"derivedFrom":makeQuery(id+"F3.opExtrude","SWEPT_BODY",BODY,{"disambiguationData":[OSD([sQuery(id+"F2.wireOp",EDGE,"E6"),sQuery(id+"F2.wireOp",EDGE,"E7"),sQuery(id+"F2.wireOp",EDGE,"E8"),sQuery(id+"F2.wireOp",EDGE,"E9.filletArc"),sQuery(id+"F2.wireOp",EDGE,"E10.MirrorCS"),sQuery(id+"F2.wireOp",EDGE,"E11.MirrorCS"),sQuery(id+"F2.wireOp",EDGE,"E12.MirrorCS"),sQuery(id+"F2.wireOp",EDGE,"E13.MirrorCS"),sQuery(id+"F2.wireOp",EDGE,"E14.1.0"),sQuery(id+"F2.wireOp",EDGE,"E14.1.1"),sQuery(id+"F2.wireOp",EDGE,"E14.1.2"),sQuery(id+"F2.wireOp",EDGE,"E14.1.3"),sQuery(id+"F2.wireOp",EDGE,"E14.1.4"),sQuery(id+"F2.wireOp",EDGE,"E14.1.5"),sQuery(id+"F2.wireOp",EDGE,"E14.1.6"),sQuery(id+"F2.wireOp",EDGE,"E14.1.7"),sQuery(id+"F2.wireOp",EDGE,"E14.2.0"),sQuery(id+"F2.wireOp",EDGE,"E14.2.1"),sQuery(id+"F2.wireOp",EDGE,"E14.2.2"),sQuery(id+"F2.wireOp",EDGE,"E14.2.3"),sQuery(id+"F2.wireOp",EDGE,"E14.2.4"),sQuery(id+"F2.wireOp",EDGE,"E14.2.5"),sQuery(id+"F2.wireOp",EDGE,"E14.2.6"),sQuery(id+"F2.wireOp",EDGE,"E14.2.7"),sQuery(id+"F2.wireOp",EDGE,"E14.3.0"),sQuery(id+"F2.wireOp",EDGE,"E14.3.1"),sQuery(id+"F2.wireOp",EDGE,"E14.3.2"),sQuery(id+"F2.wireOp",EDGE,"E14.3.3"),sQuery(id+"F2.wireOp",EDGE,"E14.3.4"),sQuery(id+"F2.wireOp",EDGE,"E14.3.5"),sQuery(id+"F2.wireOp",EDGE,"E14.3.6"),sQuery(id+"F2.wireOp",EDGE,"E14.3.7"),sQuery(id+"F2.wireOp",EDGE,"E14.4.0"),sQuery(id+"F2.wireOp",EDGE,"E14.4.1"),sQuery(id+"F2.wireOp",EDGE,"E14.4.2"),sQuery(id+"F2.wireOp",EDGE,"E14.4.3"),sQuery(id+"F2.wireOp",EDGE,"E14.4.4"),sQuery(id+"F2.wireOp",EDGE,"E14.4.5"),sQuery(id+"F2.wireOp",EDGE,"E14.4.6"),sQuery(id+"F2.wireOp",EDGE,"E14.4.7"),sQuery(id+"F2.wireOp",EDGE,"E14.5.0"),sQuery(id+"F2.wireOp",EDGE,"E14.5.1"),sQuery(id+"F2.wireOp",EDGE,"E14.5.2"),sQuery(id+"F2.wireOp",EDGE,"E14.5.3"),sQuery(id+"F2.wireOp",EDGE,"E14.5.4"),sQuery(id+"F2.wireOp",EDGE,"E14.5.5"),sQuery(id+"F2.wireOp",EDGE,"E14.5.6"),sQuery(id+"F2.wireOp",EDGE,"E14.5.7"),sQuery(id+"F2.wireOp",EDGE,"E14.6.0"),sQuery(id+"F2.wireOp",EDGE,"E14.6.1"),sQuery(id+"F2.wireOp",EDGE,"E14.6.2"),sQuery(id+"F2.wireOp",EDGE,"E14.6.3"),sQuery(id+"F2.wireOp",EDGE,"E14.6.4"),sQuery(id+"F2.wireOp",EDGE,"E14.6.5"),sQuery(id+"F2.wireOp",EDGE,"E14.6.6"),sQuery(id+"F2.wireOp",EDGE,"E14.6.7"),sQuery(id+"F2.wireOp",EDGE,"E14.7.0"),sQuery(id+"F2.wireOp",EDGE,"E14.7.1"),sQuery(id+"F2.wireOp",EDGE,"E14.7.2"),sQuery(id+"F2.wireOp",EDGE,"E14.7.3"),sQuery(id+"F2.wireOp",EDGE,"E14.7.4"),sQuery(id+"F2.wireOp",EDGE,"E14.7.5"),sQuery(id+"F2.wireOp",EDGE,"E14.7.6"),sQuery(id+"F2.wireOp",EDGE,"E14.7.7"),sQuery(id+"F2.wireOp",EDGE,"E14.8.0"),sQuery(id+"F2.wireOp",EDGE,"E14.8.1"),sQuery(id+"F2.wireOp",EDGE,"E14.8.2"),sQuery(id+"F2.wireOp",EDGE,"E14.8.3"),sQuery(id+"F2.wireOp",EDGE,"E14.8.4"),sQuery(id+"F2.wireOp",EDGE,"E14.8.5"),sQuery(id+"F2.wireOp",EDGE,"E14.8.6"),sQuery(id+"F2.wireOp",EDGE,"E14.8.7"),sQuery(id+"F2.wireOp",EDGE,"E14.9.0"),sQuery(id+"F2.wireOp",EDGE,"E14.9.1"),sQuery(id+"F2.wireOp",EDGE,"E14.9.2"),sQuery(id+"F2.wireOp",EDGE,"E14.9.3"),sQuery(id+"F2.wireOp",EDGE,"E14.9.4"),sQuery(id+"F2.wireOp",EDGE,"E14.9.5"),sQuery(id+"F2.wireOp",EDGE,"E14.9.6"),sQuery(id+"F2.wireOp",EDGE,"E14.9.7")])]}),"instanceName":"1"}),"instanceName":"1"});
            var Q1;
            Q1=sQuery(id+"F17.wireOp",EDGE,"E34");
            transform(context, id + "F22", {"entities" : qUnion([Q0]), "transformType" : TransformType.ROTATION, "transformAxis" : qUnion([Q1]), "angle" : 24 * degree, "makeCopy" : false});
        }
        {
            var Q0;
            Q0=makeQuery(id+"F3.opExtrude","SWEPT_BODY",BODY,{"disambiguationData":[OSD([sQuery(id+"F2.wireOp",EDGE,"E6"),sQuery(id+"F2.wireOp",EDGE,"E7"),sQuery(id+"F2.wireOp",EDGE,"E8"),sQuery(id+"F2.wireOp",EDGE,"E9.filletArc"),sQuery(id+"F2.wireOp",EDGE,"E10.MirrorCS"),sQuery(id+"F2.wireOp",EDGE,"E11.MirrorCS"),sQuery(id+"F2.wireOp",EDGE,"E12.MirrorCS"),sQuery(id+"F2.wireOp",EDGE,"E13.MirrorCS"),sQuery(id+"F2.wireOp",EDGE,"E14.1.0"),sQuery(id+"F2.wireOp",EDGE,"E14.1.1"),sQuery(id+"F2.wireOp",EDGE,"E14.1.2"),sQuery(id+"F2.wireOp",EDGE,"E14.1.3"),sQuery(id+"F2.wireOp",EDGE,"E14.1.4"),sQuery(id+"F2.wireOp",EDGE,"E14.1.5"),sQuery(id+"F2.wireOp",EDGE,"E14.1.6"),sQuery(id+"F2.wireOp",EDGE,"E14.1.7"),sQuery(id+"F2.wireOp",EDGE,"E14.2.0"),sQuery(id+"F2.wireOp",EDGE,"E14.2.1"),sQuery(id+"F2.wireOp",EDGE,"E14.2.2"),sQuery(id+"F2.wireOp",EDGE,"E14.2.3"),sQuery(id+"F2.wireOp",EDGE,"E14.2.4"),sQuery(id+"F2.wireOp",EDGE,"E14.2.5"),sQuery(id+"F2.wireOp",EDGE,"E14.2.6"),sQuery(id+"F2.wireOp",EDGE,"E14.2.7"),sQuery(id+"F2.wireOp",EDGE,"E14.3.0"),sQuery(id+"F2.wireOp",EDGE,"E14.3.1"),sQuery(id+"F2.wireOp",EDGE,"E14.3.2"),sQuery(id+"F2.wireOp",EDGE,"E14.3.3"),sQuery(id+"F2.wireOp",EDGE,"E14.3.4"),sQuery(id+"F2.wireOp",EDGE,"E14.3.5"),sQuery(id+"F2.wireOp",EDGE,"E14.3.6"),sQuery(id+"F2.wireOp",EDGE,"E14.3.7"),sQuery(id+"F2.wireOp",EDGE,"E14.4.0"),sQuery(id+"F2.wireOp",EDGE,"E14.4.1"),sQuery(id+"F2.wireOp",EDGE,"E14.4.2"),sQuery(id+"F2.wireOp",EDGE,"E14.4.3"),sQuery(id+"F2.wireOp",EDGE,"E14.4.4"),sQuery(id+"F2.wireOp",EDGE,"E14.4.5"),sQuery(id+"F2.wireOp",EDGE,"E14.4.6"),sQuery(id+"F2.wireOp",EDGE,"E14.4.7"),sQuery(id+"F2.wireOp",EDGE,"E14.5.0"),sQuery(id+"F2.wireOp",EDGE,"E14.5.1"),sQuery(id+"F2.wireOp",EDGE,"E14.5.2"),sQuery(id+"F2.wireOp",EDGE,"E14.5.3"),sQuery(id+"F2.wireOp",EDGE,"E14.5.4"),sQuery(id+"F2.wireOp",EDGE,"E14.5.5"),sQuery(id+"F2.wireOp",EDGE,"E14.5.6"),sQuery(id+"F2.wireOp",EDGE,"E14.5.7"),sQuery(id+"F2.wireOp",EDGE,"E14.6.0"),sQuery(id+"F2.wireOp",EDGE,"E14.6.1"),sQuery(id+"F2.wireOp",EDGE,"E14.6.2"),sQuery(id+"F2.wireOp",EDGE,"E14.6.3"),sQuery(id+"F2.wireOp",EDGE,"E14.6.4"),sQuery(id+"F2.wireOp",EDGE,"E14.6.5"),sQuery(id+"F2.wireOp",EDGE,"E14.6.6"),sQuery(id+"F2.wireOp",EDGE,"E14.6.7"),sQuery(id+"F2.wireOp",EDGE,"E14.7.0"),sQuery(id+"F2.wireOp",EDGE,"E14.7.1"),sQuery(id+"F2.wireOp",EDGE,"E14.7.2"),sQuery(id+"F2.wireOp",EDGE,"E14.7.3"),sQuery(id+"F2.wireOp",EDGE,"E14.7.4"),sQuery(id+"F2.wireOp",EDGE,"E14.7.5"),sQuery(id+"F2.wireOp",EDGE,"E14.7.6"),sQuery(id+"F2.wireOp",EDGE,"E14.7.7"),sQuery(id+"F2.wireOp",EDGE,"E14.8.0"),sQuery(id+"F2.wireOp",EDGE,"E14.8.1"),sQuery(id+"F2.wireOp",EDGE,"E14.8.2"),sQuery(id+"F2.wireOp",EDGE,"E14.8.3"),sQuery(id+"F2.wireOp",EDGE,"E14.8.4"),sQuery(id+"F2.wireOp",EDGE,"E14.8.5"),sQuery(id+"F2.wireOp",EDGE,"E14.8.6"),sQuery(id+"F2.wireOp",EDGE,"E14.8.7"),sQuery(id+"F2.wireOp",EDGE,"E14.9.0"),sQuery(id+"F2.wireOp",EDGE,"E14.9.1"),sQuery(id+"F2.wireOp",EDGE,"E14.9.2"),sQuery(id+"F2.wireOp",EDGE,"E14.9.3"),sQuery(id+"F2.wireOp",EDGE,"E14.9.4"),sQuery(id+"F2.wireOp",EDGE,"E14.9.5"),sQuery(id+"F2.wireOp",EDGE,"E14.9.6"),sQuery(id+"F2.wireOp",EDGE,"E14.9.7")])]});
            var Q1;
            Q1=sQuery(id+"F19.wireOp",EDGE,"E36");
            transform(context, id + "F23", {"entities" : qUnion([Q0]), "transformType" : TransformType.TRANSLATION_ENTITY, "oppositeDirectionEntity" : false, "transformLine" : qUnion([Q1]), "makeCopy" : false});
        }
        {
            var Q0;
            Q0=makeQuery(id+"F6.opPattern","COPY",BODY,{"derivedFrom":makeQuery(id+"F3.opExtrude","SWEPT_BODY",BODY,{"disambiguationData":[OSD([sQuery(id+"F2.wireOp",EDGE,"E6"),sQuery(id+"F2.wireOp",EDGE,"E7"),sQuery(id+"F2.wireOp",EDGE,"E8"),sQuery(id+"F2.wireOp",EDGE,"E9.filletArc"),sQuery(id+"F2.wireOp",EDGE,"E10.MirrorCS"),sQuery(id+"F2.wireOp",EDGE,"E11.MirrorCS"),sQuery(id+"F2.wireOp",EDGE,"E12.MirrorCS"),sQuery(id+"F2.wireOp",EDGE,"E13.MirrorCS"),sQuery(id+"F2.wireOp",EDGE,"E14.1.0"),sQuery(id+"F2.wireOp",EDGE,"E14.1.1"),sQuery(id+"F2.wireOp",EDGE,"E14.1.2"),sQuery(id+"F2.wireOp",EDGE,"E14.1.3"),sQuery(id+"F2.wireOp",EDGE,"E14.1.4"),sQuery(id+"F2.wireOp",EDGE,"E14.1.5"),sQuery(id+"F2.wireOp",EDGE,"E14.1.6"),sQuery(id+"F2.wireOp",EDGE,"E14.1.7"),sQuery(id+"F2.wireOp",EDGE,"E14.2.0"),sQuery(id+"F2.wireOp",EDGE,"E14.2.1"),sQuery(id+"F2.wireOp",EDGE,"E14.2.2"),sQuery(id+"F2.wireOp",EDGE,"E14.2.3"),sQuery(id+"F2.wireOp",EDGE,"E14.2.4"),sQuery(id+"F2.wireOp",EDGE,"E14.2.5"),sQuery(id+"F2.wireOp",EDGE,"E14.2.6"),sQuery(id+"F2.wireOp",EDGE,"E14.2.7"),sQuery(id+"F2.wireOp",EDGE,"E14.3.0"),sQuery(id+"F2.wireOp",EDGE,"E14.3.1"),sQuery(id+"F2.wireOp",EDGE,"E14.3.2"),sQuery(id+"F2.wireOp",EDGE,"E14.3.3"),sQuery(id+"F2.wireOp",EDGE,"E14.3.4"),sQuery(id+"F2.wireOp",EDGE,"E14.3.5"),sQuery(id+"F2.wireOp",EDGE,"E14.3.6"),sQuery(id+"F2.wireOp",EDGE,"E14.3.7"),sQuery(id+"F2.wireOp",EDGE,"E14.4.0"),sQuery(id+"F2.wireOp",EDGE,"E14.4.1"),sQuery(id+"F2.wireOp",EDGE,"E14.4.2"),sQuery(id+"F2.wireOp",EDGE,"E14.4.3"),sQuery(id+"F2.wireOp",EDGE,"E14.4.4"),sQuery(id+"F2.wireOp",EDGE,"E14.4.5"),sQuery(id+"F2.wireOp",EDGE,"E14.4.6"),sQuery(id+"F2.wireOp",EDGE,"E14.4.7"),sQuery(id+"F2.wireOp",EDGE,"E14.5.0"),sQuery(id+"F2.wireOp",EDGE,"E14.5.1"),sQuery(id+"F2.wireOp",EDGE,"E14.5.2"),sQuery(id+"F2.wireOp",EDGE,"E14.5.3"),sQuery(id+"F2.wireOp",EDGE,"E14.5.4"),sQuery(id+"F2.wireOp",EDGE,"E14.5.5"),sQuery(id+"F2.wireOp",EDGE,"E14.5.6"),sQuery(id+"F2.wireOp",EDGE,"E14.5.7"),sQuery(id+"F2.wireOp",EDGE,"E14.6.0"),sQuery(id+"F2.wireOp",EDGE,"E14.6.1"),sQuery(id+"F2.wireOp",EDGE,"E14.6.2"),sQuery(id+"F2.wireOp",EDGE,"E14.6.3"),sQuery(id+"F2.wireOp",EDGE,"E14.6.4"),sQuery(id+"F2.wireOp",EDGE,"E14.6.5"),sQuery(id+"F2.wireOp",EDGE,"E14.6.6"),sQuery(id+"F2.wireOp",EDGE,"E14.6.7"),sQuery(id+"F2.wireOp",EDGE,"E14.7.0"),sQuery(id+"F2.wireOp",EDGE,"E14.7.1"),sQuery(id+"F2.wireOp",EDGE,"E14.7.2"),sQuery(id+"F2.wireOp",EDGE,"E14.7.3"),sQuery(id+"F2.wireOp",EDGE,"E14.7.4"),sQuery(id+"F2.wireOp",EDGE,"E14.7.5"),sQuery(id+"F2.wireOp",EDGE,"E14.7.6"),sQuery(id+"F2.wireOp",EDGE,"E14.7.7"),sQuery(id+"F2.wireOp",EDGE,"E14.8.0"),sQuery(id+"F2.wireOp",EDGE,"E14.8.1"),sQuery(id+"F2.wireOp",EDGE,"E14.8.2"),sQuery(id+"F2.wireOp",EDGE,"E14.8.3"),sQuery(id+"F2.wireOp",EDGE,"E14.8.4"),sQuery(id+"F2.wireOp",EDGE,"E14.8.5"),sQuery(id+"F2.wireOp",EDGE,"E14.8.6"),sQuery(id+"F2.wireOp",EDGE,"E14.8.7"),sQuery(id+"F2.wireOp",EDGE,"E14.9.0"),sQuery(id+"F2.wireOp",EDGE,"E14.9.1"),sQuery(id+"F2.wireOp",EDGE,"E14.9.2"),sQuery(id+"F2.wireOp",EDGE,"E14.9.3"),sQuery(id+"F2.wireOp",EDGE,"E14.9.4"),sQuery(id+"F2.wireOp",EDGE,"E14.9.5"),sQuery(id+"F2.wireOp",EDGE,"E14.9.6"),sQuery(id+"F2.wireOp",EDGE,"E14.9.7")])]}),"instanceName":"1"});
            var Q1;
            Q1=sQuery(id+"F19.wireOp",EDGE,"E37");
            transform(context, id + "F24", {"entities" : qUnion([Q0]), "transformType" : TransformType.TRANSLATION_ENTITY, "oppositeDirectionEntity" : false, "transformLine" : qUnion([Q1]), "makeCopy" : false});
        }
        {
            var Q0;
            Q0=makeQuery(id+"F11.opPattern","COPY",BODY,{"derivedFrom":makeQuery(id+"F6.opPattern","COPY",BODY,{"derivedFrom":makeQuery(id+"F3.opExtrude","SWEPT_BODY",BODY,{"disambiguationData":[OSD([sQuery(id+"F2.wireOp",EDGE,"E6"),sQuery(id+"F2.wireOp",EDGE,"E7"),sQuery(id+"F2.wireOp",EDGE,"E8"),sQuery(id+"F2.wireOp",EDGE,"E9.filletArc"),sQuery(id+"F2.wireOp",EDGE,"E10.MirrorCS"),sQuery(id+"F2.wireOp",EDGE,"E11.MirrorCS"),sQuery(id+"F2.wireOp",EDGE,"E12.MirrorCS"),sQuery(id+"F2.wireOp",EDGE,"E13.MirrorCS"),sQuery(id+"F2.wireOp",EDGE,"E14.1.0"),sQuery(id+"F2.wireOp",EDGE,"E14.1.1"),sQuery(id+"F2.wireOp",EDGE,"E14.1.2"),sQuery(id+"F2.wireOp",EDGE,"E14.1.3"),sQuery(id+"F2.wireOp",EDGE,"E14.1.4"),sQuery(id+"F2.wireOp",EDGE,"E14.1.5"),sQuery(id+"F2.wireOp",EDGE,"E14.1.6"),sQuery(id+"F2.wireOp",EDGE,"E14.1.7"),sQuery(id+"F2.wireOp",EDGE,"E14.2.0"),sQuery(id+"F2.wireOp",EDGE,"E14.2.1"),sQuery(id+"F2.wireOp",EDGE,"E14.2.2"),sQuery(id+"F2.wireOp",EDGE,"E14.2.3"),sQuery(id+"F2.wireOp",EDGE,"E14.2.4"),sQuery(id+"F2.wireOp",EDGE,"E14.2.5"),sQuery(id+"F2.wireOp",EDGE,"E14.2.6"),sQuery(id+"F2.wireOp",EDGE,"E14.2.7"),sQuery(id+"F2.wireOp",EDGE,"E14.3.0"),sQuery(id+"F2.wireOp",EDGE,"E14.3.1"),sQuery(id+"F2.wireOp",EDGE,"E14.3.2"),sQuery(id+"F2.wireOp",EDGE,"E14.3.3"),sQuery(id+"F2.wireOp",EDGE,"E14.3.4"),sQuery(id+"F2.wireOp",EDGE,"E14.3.5"),sQuery(id+"F2.wireOp",EDGE,"E14.3.6"),sQuery(id+"F2.wireOp",EDGE,"E14.3.7"),sQuery(id+"F2.wireOp",EDGE,"E14.4.0"),sQuery(id+"F2.wireOp",EDGE,"E14.4.1"),sQuery(id+"F2.wireOp",EDGE,"E14.4.2"),sQuery(id+"F2.wireOp",EDGE,"E14.4.3"),sQuery(id+"F2.wireOp",EDGE,"E14.4.4"),sQuery(id+"F2.wireOp",EDGE,"E14.4.5"),sQuery(id+"F2.wireOp",EDGE,"E14.4.6"),sQuery(id+"F2.wireOp",EDGE,"E14.4.7"),sQuery(id+"F2.wireOp",EDGE,"E14.5.0"),sQuery(id+"F2.wireOp",EDGE,"E14.5.1"),sQuery(id+"F2.wireOp",EDGE,"E14.5.2"),sQuery(id+"F2.wireOp",EDGE,"E14.5.3"),sQuery(id+"F2.wireOp",EDGE,"E14.5.4"),sQuery(id+"F2.wireOp",EDGE,"E14.5.5"),sQuery(id+"F2.wireOp",EDGE,"E14.5.6"),sQuery(id+"F2.wireOp",EDGE,"E14.5.7"),sQuery(id+"F2.wireOp",EDGE,"E14.6.0"),sQuery(id+"F2.wireOp",EDGE,"E14.6.1"),sQuery(id+"F2.wireOp",EDGE,"E14.6.2"),sQuery(id+"F2.wireOp",EDGE,"E14.6.3"),sQuery(id+"F2.wireOp",EDGE,"E14.6.4"),sQuery(id+"F2.wireOp",EDGE,"E14.6.5"),sQuery(id+"F2.wireOp",EDGE,"E14.6.6"),sQuery(id+"F2.wireOp",EDGE,"E14.6.7"),sQuery(id+"F2.wireOp",EDGE,"E14.7.0"),sQuery(id+"F2.wireOp",EDGE,"E14.7.1"),sQuery(id+"F2.wireOp",EDGE,"E14.7.2"),sQuery(id+"F2.wireOp",EDGE,"E14.7.3"),sQuery(id+"F2.wireOp",EDGE,"E14.7.4"),sQuery(id+"F2.wireOp",EDGE,"E14.7.5"),sQuery(id+"F2.wireOp",EDGE,"E14.7.6"),sQuery(id+"F2.wireOp",EDGE,"E14.7.7"),sQuery(id+"F2.wireOp",EDGE,"E14.8.0"),sQuery(id+"F2.wireOp",EDGE,"E14.8.1"),sQuery(id+"F2.wireOp",EDGE,"E14.8.2"),sQuery(id+"F2.wireOp",EDGE,"E14.8.3"),sQuery(id+"F2.wireOp",EDGE,"E14.8.4"),sQuery(id+"F2.wireOp",EDGE,"E14.8.5"),sQuery(id+"F2.wireOp",EDGE,"E14.8.6"),sQuery(id+"F2.wireOp",EDGE,"E14.8.7"),sQuery(id+"F2.wireOp",EDGE,"E14.9.0"),sQuery(id+"F2.wireOp",EDGE,"E14.9.1"),sQuery(id+"F2.wireOp",EDGE,"E14.9.2"),sQuery(id+"F2.wireOp",EDGE,"E14.9.3"),sQuery(id+"F2.wireOp",EDGE,"E14.9.4"),sQuery(id+"F2.wireOp",EDGE,"E14.9.5"),sQuery(id+"F2.wireOp",EDGE,"E14.9.6"),sQuery(id+"F2.wireOp",EDGE,"E14.9.7")])]}),"instanceName":"1"}),"instanceName":"1"});
            var Q1;
            Q1=sQuery(id+"F19.wireOp",EDGE,"E38");
            transform(context, id + "F25", {"entities" : qUnion([Q0]), "transformType" : TransformType.TRANSLATION_ENTITY, "oppositeDirectionEntity" : false, "transformLine" : qUnion([Q1]), "makeCopy" : false});
        }
        {
            var Q0;
            Q0=qCreatedBy(makeId("Top.planeOp"),FACE);
            cPlane(context, id + "F26", {"entities" : qUnion([Q0]), "cplaneType" : CPlaneType.OFFSET, "offset" : 0.3 * mm, "oppositeDirection" : true, "width" : 150 * mm, "height" : 150 * mm});
        }
        {
            var Q0;
            Q0=qCreatedBy(id+"F26.planeOp",FACE);
            var sketch = newSketch(context, id + "F27", { "sketchPlane" : qUnion([Q0])});
            skCircle(sketch, "E39", {"center": v(0, 0) * mm, "radius": 9.25 * mm});
            skCircle(sketch, "E40", {"center": v(0, 0) * mm, "radius": 5.25 * mm});
            skSolve(sketch);
        }
        {
            var Q0;
            Q0=qSketchRegion(id+"F27",true);
            extrude(context, id + "F28", {"entities" : qUnion([Q0]), "oppositeDirection" : true, "depth" : 1.6 * mm});
        }
    });
